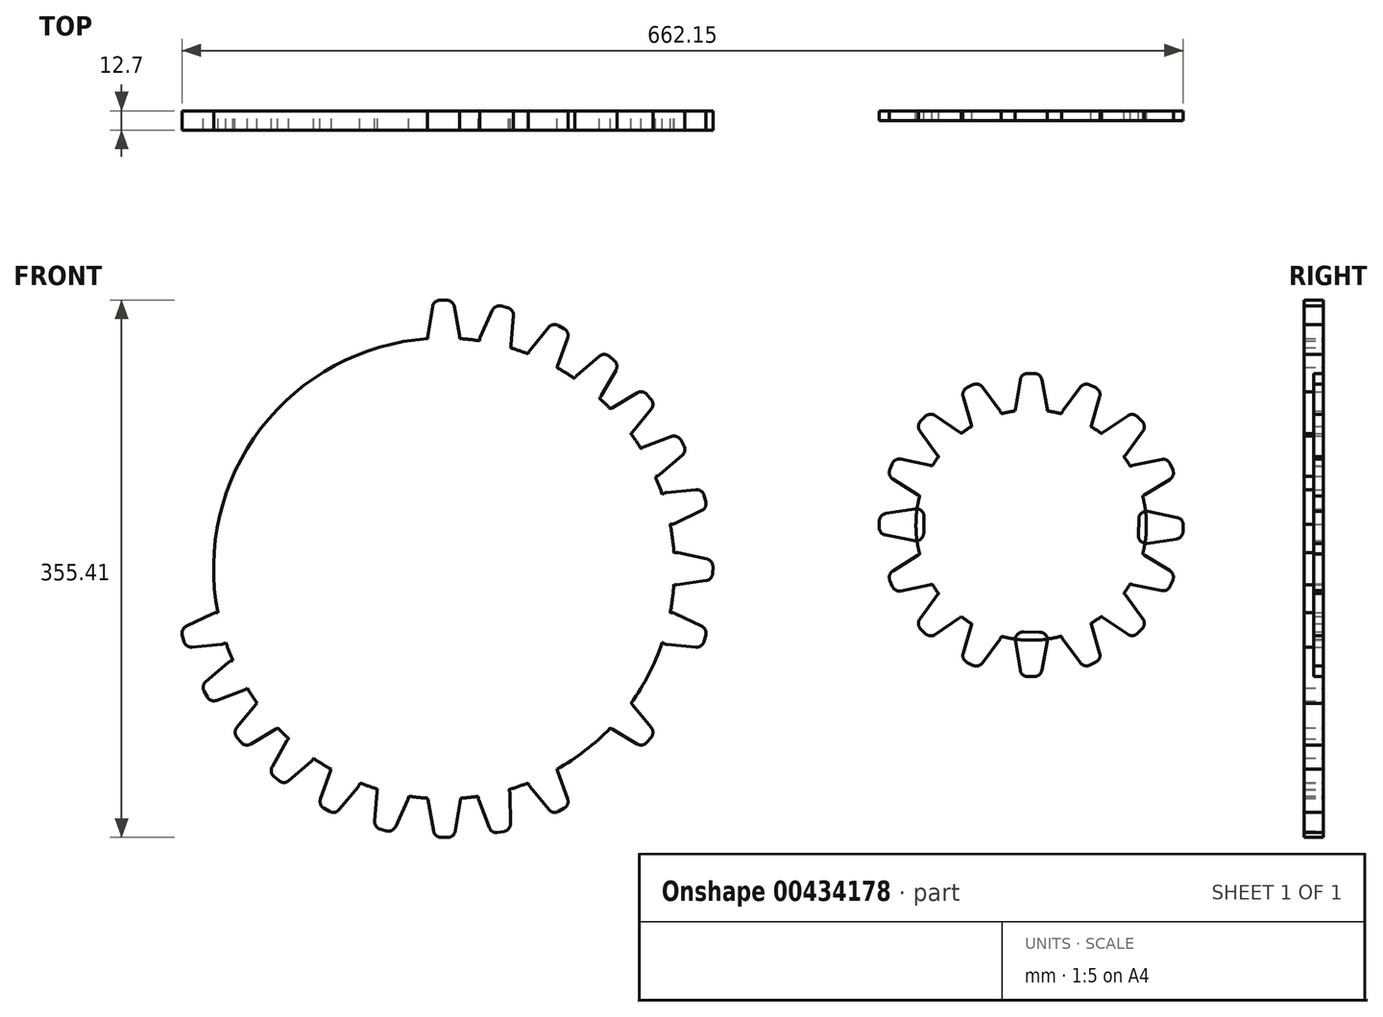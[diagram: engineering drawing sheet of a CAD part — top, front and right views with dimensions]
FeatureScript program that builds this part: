
annotation { "Feature Type Name" : "Feature", "Feature Type Description" : "" }
export const myFeature = defineFeature(function(context is Context, id is Id, definition is map)
    precondition{}
    {
        {
            var Q0;
            Q0=qCreatedBy(makeId("Front.planeOp"),FACE);
            var sketch = newSketch(context, id + "F0", { "sketchPlane" : qUnion([Q0])});
            skCircle(sketch, "E0", {"center": v(0, 0) * mm, "radius": 6.35 * mm});
            skCircle(sketch, "E1", {"center": v(0, 0) * mm, "radius": 152.4 * mm});
            skCircle(sketch, "E2", {"center": v(388.27, 28.72) * mm, "radius": 6.35 * mm});
            skCircle(sketch, "E3", {"center": v(388.27, 28.72) * mm, "radius": 76.2 * mm});
            skLineSegment(sketch, "E4", {"start": v(0, 0) * mm, "end": v(0, -152.4) * mm});
            skLineSegment(sketch, "E5", {"start": v(0, 0) * mm, "end": v(152.4, 0) * mm});
            skLineSegment(sketch, "E6", {"start": v(0, 0) * mm, "end": v(-152.4, 0) * mm});
            skLineSegment(sketch, "E7", {"start": v(37.99, 173.6) * mm, "end": v(42.15, 172.48) * mm});
            skLineSegment(sketch, "E8", {"start": v(45.9, 167.19) * mm, "end": v(44.4, 147.67) * mm});
            skLineSegment(sketch, "E9", {"start": v(32.05, 170.78) * mm, "end": v(23.95, 152.91) * mm});
            skLineSegment(sketch, "E10", {"start": v(27.31, 145.9) * mm, "end": v(38.08, 143.14) * mm});
            skPoint(sketch, "E11.visualSharp", {"position": v(33.82, 174.7) * mm});
            skArc(sketch, "E11.filletArc", {"start": v(37.99, 173.6) * mm, "mid": v(34.5, 173.28) * mm, "end": v(32.05, 170.78) * mm});
            skPoint(sketch, "E12.visualSharp", {"position": v(46.22, 171.39) * mm});
            skArc(sketch, "E12.filletArc", {"start": v(45.9, 167.19) * mm, "mid": v(44.98, 170.5) * mm, "end": v(42.15, 172.48) * mm});
            skPoint(sketch, "E13.visualSharp", {"position": v(43.94, 141.63) * mm});
            skArc(sketch, "E13.filletArc", {"start": v(38.08, 143.14) * mm, "mid": v(42.3, 143.93) * mm, "end": v(44.4, 147.67) * mm});
            skPoint(sketch, "E14.visualSharp", {"position": v(21.45, 147.4) * mm});
            skArc(sketch, "E14.filletArc", {"start": v(23.95, 152.91) * mm, "mid": v(24, 148.62) * mm, "end": v(27.31, 145.9) * mm});
            skPoint(sketch, "E15.endSnap0", {"position": v(32.7, 144.51) * mm});
            skLineSegment(sketch, "E16", {"start": v(75.72, 160.72) * mm, "end": v(79.45, 158.56) * mm});
            skLineSegment(sketch, "E17", {"start": v(81.7, 152.48) * mm, "end": v(75.21, 134.01) * mm});
            skLineSegment(sketch, "E18", {"start": v(69.26, 159.54) * mm, "end": v(56.8, 144.37) * mm});
            skLineSegment(sketch, "E19", {"start": v(58.24, 136.72) * mm, "end": v(67.93, 131.27) * mm});
            skPoint(sketch, "E20.visualSharp", {"position": v(71.99, 162.87) * mm});
            skArc(sketch, "E20.filletArc", {"start": v(75.72, 160.72) * mm, "mid": v(72.27, 161.31) * mm, "end": v(69.26, 159.54) * mm});
            skPoint(sketch, "E21.visualSharp", {"position": v(83.1, 156.46) * mm});
            skArc(sketch, "E21.filletArc", {"start": v(81.7, 152.48) * mm, "mid": v(81.68, 155.93) * mm, "end": v(79.45, 158.56) * mm});
            skPoint(sketch, "E22.visualSharp", {"position": v(73.2, 128.3) * mm});
            skArc(sketch, "E22.filletArc", {"start": v(67.93, 131.27) * mm, "mid": v(72.2, 130.94) * mm, "end": v(75.21, 134.01) * mm});
            skPoint(sketch, "E23.visualSharp", {"position": v(52.97, 139.7) * mm});
            skArc(sketch, "E23.filletArc", {"start": v(56.8, 144.37) * mm, "mid": v(55.74, 140.21) * mm, "end": v(58.24, 136.72) * mm});
            skPoint(sketch, "E24.endSnap0", {"position": v(63.08, 134) * mm});
            skLineSegment(sketch, "E25", {"start": v(109.2, 140.37) * mm, "end": v(112.5, 137.6) * mm});
            skLineSegment(sketch, "E26", {"start": v(113.66, 131.22) * mm, "end": v(104.06, 114.16) * mm});
            skLineSegment(sketch, "E27", {"start": v(102.63, 140.33) * mm, "end": v(87.74, 127.56) * mm});
            skLineSegment(sketch, "E28", {"start": v(87.82, 119.78) * mm, "end": v(96.41, 112.73) * mm});
            skPoint(sketch, "E29.visualSharp", {"position": v(105.9, 143.14) * mm});
            skArc(sketch, "E29.filletArc", {"start": v(109.2, 140.37) * mm, "mid": v(105.91, 141.56) * mm, "end": v(102.63, 140.33) * mm});
            skPoint(sketch, "E30.visualSharp", {"position": v(115.73, 134.9) * mm});
            skArc(sketch, "E30.filletArc", {"start": v(113.66, 131.22) * mm, "mid": v(114.24, 134.62) * mm, "end": v(112.5, 137.6) * mm});
            skPoint(sketch, "E31.visualSharp", {"position": v(101.1, 108.89) * mm});
            skArc(sketch, "E31.filletArc", {"start": v(96.41, 112.73) * mm, "mid": v(100.57, 111.66) * mm, "end": v(104.06, 114.16) * mm});
            skPoint(sketch, "E32.visualSharp", {"position": v(83.14, 123.62) * mm});
            skArc(sketch, "E32.filletArc", {"start": v(87.74, 127.56) * mm, "mid": v(85.97, 123.65) * mm, "end": v(87.82, 119.78) * mm});
            skPoint(sketch, "E33.endSnap0", {"position": v(92.12, 116.25) * mm});
            skLineSegment(sketch, "E34", {"start": v(134.2, 115.06) * mm, "end": v(136.96, 111.76) * mm});
            skLineSegment(sketch, "E35", {"start": v(137, 105.27) * mm, "end": v(124.58, 90.14) * mm});
            skLineSegment(sketch, "E36", {"start": v(127.72, 116.16) * mm, "end": v(110.83, 106.17) * mm});
            skLineSegment(sketch, "E37", {"start": v(109.56, 98.49) * mm, "end": v(116.8, 90.06) * mm});
            skPoint(sketch, "E38.visualSharp", {"position": v(131.42, 118.36) * mm});
            skArc(sketch, "E38.filletArc", {"start": v(134.2, 115.06) * mm, "mid": v(131.16, 116.8) * mm, "end": v(127.72, 116.16) * mm});
            skPoint(sketch, "E39.visualSharp", {"position": v(139.67, 108.53) * mm});
            skArc(sketch, "E39.filletArc", {"start": v(137, 105.27) * mm, "mid": v(138.15, 108.52) * mm, "end": v(136.96, 111.76) * mm});
            skPoint(sketch, "E40.visualSharp", {"position": v(120.74, 85.46) * mm});
            skArc(sketch, "E40.filletArc", {"start": v(116.8, 90.06) * mm, "mid": v(120.7, 88.28) * mm, "end": v(124.58, 90.14) * mm});
            skPoint(sketch, "E41.visualSharp", {"position": v(105.62, 103.08) * mm});
            skArc(sketch, "E41.filletArc", {"start": v(110.83, 106.17) * mm, "mid": v(108.4, 102.62) * mm, "end": v(109.56, 98.49) * mm});
            skPoint(sketch, "E42.endSnap0", {"position": v(113.18, 94.27) * mm});
            skLineSegment(sketch, "E43", {"start": v(156.51, 85.04) * mm, "end": v(158.66, 81.31) * mm});
            skLineSegment(sketch, "E44", {"start": v(157.57, 74.92) * mm, "end": v(142.72, 62.17) * mm});
            skLineSegment(sketch, "E45", {"start": v(150.32, 87.26) * mm, "end": v(131.96, 80.34) * mm});
            skLineSegment(sketch, "E46", {"start": v(129.38, 73) * mm, "end": v(135.04, 63.44) * mm});
            skPoint(sketch, "E47.visualSharp", {"position": v(154.36, 88.77) * mm});
            skArc(sketch, "E47.filletArc", {"start": v(156.51, 85.04) * mm, "mid": v(153.82, 87.28) * mm, "end": v(150.32, 87.26) * mm});
            skPoint(sketch, "E48.visualSharp", {"position": v(160.77, 77.66) * mm});
            skArc(sketch, "E48.filletArc", {"start": v(157.57, 74.92) * mm, "mid": v(159.27, 77.92) * mm, "end": v(158.66, 81.31) * mm});
            skPoint(sketch, "E49.visualSharp", {"position": v(138.12, 58.23) * mm});
            skArc(sketch, "E49.filletArc", {"start": v(135.04, 63.44) * mm, "mid": v(138.58, 61.02) * mm, "end": v(142.72, 62.17) * mm});
            skPoint(sketch, "E50.visualSharp", {"position": v(126.3, 78.21) * mm});
            skArc(sketch, "E50.filletArc", {"start": v(131.96, 80.34) * mm, "mid": v(128.96, 77.27) * mm, "end": v(129.38, 73) * mm});
            skPoint(sketch, "E51.endSnap0", {"position": v(132.2, 68.22) * mm});
            skLineSegment(sketch, "E52", {"start": v(172.02, 48.32) * mm, "end": v(173.13, 44.16) * mm});
            skLineSegment(sketch, "E53", {"start": v(170.42, 38.26) * mm, "end": v(152.77, 29.8) * mm});
            skLineSegment(sketch, "E54", {"start": v(166.61, 52.06) * mm, "end": v(147.09, 50.13) * mm});
            skLineSegment(sketch, "E55", {"start": v(142.7, 43.7) * mm, "end": v(145.68, 33) * mm});
            skPoint(sketch, "E56.visualSharp", {"position": v(170.9, 52.48) * mm});
            skArc(sketch, "E56.filletArc", {"start": v(172.02, 48.32) * mm, "mid": v(170, 51.18) * mm, "end": v(166.61, 52.06) * mm});
            skPoint(sketch, "E57.visualSharp", {"position": v(174.22, 40.08) * mm});
            skArc(sketch, "E57.filletArc", {"start": v(170.42, 38.26) * mm, "mid": v(172.84, 40.72) * mm, "end": v(173.13, 44.16) * mm});
            skPoint(sketch, "E58.visualSharp", {"position": v(147.31, 27.18) * mm});
            skArc(sketch, "E58.filletArc", {"start": v(145.68, 33) * mm, "mid": v(148.48, 29.75) * mm, "end": v(152.77, 29.8) * mm});
            skPoint(sketch, "E59.visualSharp", {"position": v(141.06, 49.54) * mm});
            skArc(sketch, "E59.filletArc", {"start": v(147.09, 50.13) * mm, "mid": v(143.4, 47.95) * mm, "end": v(142.7, 43.7) * mm});
            skPoint(sketch, "E60.endSnap0", {"position": v(144.19, 38.36) * mm});
            skArc(sketch, "E61.MirrorCS", {"start": v(-45.9, 167.19) * mm, "mid": v(-44.98, 170.5) * mm, "end": v(-42.15, 172.48) * mm});
            skArc(sketch, "E62.MirrorCS", {"start": v(-113.66, 131.22) * mm, "mid": v(-114.24, 134.62) * mm, "end": v(-112.5, 137.6) * mm});
            skArc(sketch, "E63.MirrorCS", {"start": v(-157.57, 74.92) * mm, "mid": v(-159.27, 77.92) * mm, "end": v(-158.66, 81.31) * mm});
            skArc(sketch, "E64.MirrorCS", {"start": v(-75.72, 160.72) * mm, "mid": v(-72.27, 161.31) * mm, "end": v(-69.26, 159.54) * mm});
            skArc(sketch, "E65.MirrorCS", {"start": v(-134.2, 115.06) * mm, "mid": v(-131.16, 116.8) * mm, "end": v(-127.72, 116.16) * mm});
            skArc(sketch, "E66.MirrorCS", {"start": v(-170.42, 38.26) * mm, "mid": v(-172.84, 40.72) * mm, "end": v(-173.13, 44.16) * mm});
            skLineSegment(sketch, "E67.MirrorCS", {"start": v(-156.51, 85.04) * mm, "end": v(-158.66, 81.31) * mm});
            skLineSegment(sketch, "E68.MirrorCS", {"start": v(-134.2, 115.06) * mm, "end": v(-136.96, 111.76) * mm});
            skLineSegment(sketch, "E69.MirrorCS", {"start": v(-37.99, 173.6) * mm, "end": v(-42.15, 172.48) * mm});
            skLineSegment(sketch, "E70.MirrorCS", {"start": v(-109.2, 140.37) * mm, "end": v(-112.5, 137.6) * mm});
            skLineSegment(sketch, "E71.MirrorCS", {"start": v(-75.72, 160.72) * mm, "end": v(-79.45, 158.56) * mm});
            skLineSegment(sketch, "E72.MirrorCS", {"start": v(-172.02, 48.32) * mm, "end": v(-173.13, 44.16) * mm});
            skArc(sketch, "E73.MirrorCS", {"start": v(-109.2, 140.37) * mm, "mid": v(-105.91, 141.56) * mm, "end": v(-102.63, 140.33) * mm});
            skArc(sketch, "E74.MirrorCS", {"start": v(-137, 105.27) * mm, "mid": v(-138.15, 108.52) * mm, "end": v(-136.96, 111.76) * mm});
            skArc(sketch, "E75.MirrorCS", {"start": v(-37.99, 173.6) * mm, "mid": v(-34.5, 173.28) * mm, "end": v(-32.05, 170.78) * mm});
            skArc(sketch, "E76.MirrorCS", {"start": v(-156.51, 85.04) * mm, "mid": v(-153.82, 87.28) * mm, "end": v(-150.32, 87.26) * mm});
            skArc(sketch, "E77.MirrorCS", {"start": v(-81.7, 152.48) * mm, "mid": v(-81.68, 155.93) * mm, "end": v(-79.45, 158.56) * mm});
            skArc(sketch, "E78.MirrorCS", {"start": v(-67.93, 131.27) * mm, "mid": v(-72.2, 130.94) * mm, "end": v(-75.21, 134.01) * mm});
            skArc(sketch, "E79.MirrorCS", {"start": v(-116.8, 90.06) * mm, "mid": v(-120.7, 88.28) * mm, "end": v(-124.58, 90.14) * mm});
            skArc(sketch, "E80.MirrorCS", {"start": v(-145.68, 33) * mm, "mid": v(-148.48, 29.75) * mm, "end": v(-152.77, 29.8) * mm});
            skArc(sketch, "E81.MirrorCS", {"start": v(-135.04, 63.44) * mm, "mid": v(-138.58, 61.02) * mm, "end": v(-142.72, 62.17) * mm});
            skArc(sketch, "E82.MirrorCS", {"start": v(-96.41, 112.73) * mm, "mid": v(-100.57, 111.66) * mm, "end": v(-104.06, 114.16) * mm});
            skArc(sketch, "E83.MirrorCS", {"start": v(-38.08, 143.14) * mm, "mid": v(-42.3, 143.93) * mm, "end": v(-44.4, 147.67) * mm});
            skArc(sketch, "E84.MirrorCS", {"start": v(-147.09, 50.13) * mm, "mid": v(-143.4, 47.95) * mm, "end": v(-142.7, 43.7) * mm});
            skArc(sketch, "E85.MirrorCS", {"start": v(-110.83, 106.17) * mm, "mid": v(-108.4, 102.62) * mm, "end": v(-109.56, 98.49) * mm});
            skArc(sketch, "E86.MirrorCS", {"start": v(-56.8, 144.37) * mm, "mid": v(-55.74, 140.21) * mm, "end": v(-58.24, 136.72) * mm});
            skArc(sketch, "E87.MirrorCS", {"start": v(-172.02, 48.32) * mm, "mid": v(-170, 51.18) * mm, "end": v(-166.61, 52.06) * mm});
            skLineSegment(sketch, "E88.MirrorCS", {"start": v(-142.7, 43.7) * mm, "end": v(-145.68, 33) * mm});
            skLineSegment(sketch, "E89.MirrorCS", {"start": v(-109.56, 98.49) * mm, "end": v(-116.8, 90.06) * mm});
            skLineSegment(sketch, "E90.MirrorCS", {"start": v(-58.24, 136.72) * mm, "end": v(-67.93, 131.27) * mm});
            skLineSegment(sketch, "E91.MirrorCS", {"start": v(-27.31, 145.9) * mm, "end": v(-38.08, 143.14) * mm});
            skArc(sketch, "E92.MirrorCS", {"start": v(-87.74, 127.56) * mm, "mid": v(-85.97, 123.65) * mm, "end": v(-87.82, 119.78) * mm});
            skArc(sketch, "E93.MirrorCS", {"start": v(-23.95, 152.91) * mm, "mid": v(-24, 148.62) * mm, "end": v(-27.31, 145.9) * mm});
            skArc(sketch, "E94.MirrorCS", {"start": v(-131.96, 80.34) * mm, "mid": v(-128.96, 77.27) * mm, "end": v(-129.38, 73) * mm});
            skLineSegment(sketch, "E95.MirrorCS", {"start": v(-87.82, 119.78) * mm, "end": v(-96.41, 112.73) * mm});
            skLineSegment(sketch, "E96.MirrorCS", {"start": v(-129.38, 73) * mm, "end": v(-135.04, 63.44) * mm});
            skPoint(sketch, "E97.MirrorP", {"position": v(-132.2, 68.22) * mm});
            skPoint(sketch, "E98.MirrorP", {"position": v(-144.19, 38.36) * mm});
            skPoint(sketch, "E99.MirrorP", {"position": v(-160.77, 77.66) * mm});
            skPoint(sketch, "E100.MirrorP", {"position": v(-101.1, 108.89) * mm});
            skPoint(sketch, "E101.MirrorP", {"position": v(-21.45, 147.4) * mm});
            skPoint(sketch, "E102.MirrorP", {"position": v(-73.2, 128.3) * mm});
            skPoint(sketch, "E103.MirrorP", {"position": v(-141.06, 49.54) * mm});
            skPoint(sketch, "E104.MirrorP", {"position": v(-113.18, 94.27) * mm});
            skPoint(sketch, "E105.MirrorP", {"position": v(-71.99, 162.87) * mm});
            skPoint(sketch, "E106.MirrorP", {"position": v(-46.22, 171.39) * mm});
            skLineSegment(sketch, "E107.MirrorCS", {"start": v(-170.42, 38.26) * mm, "end": v(-152.77, 29.8) * mm});
            skPoint(sketch, "E108.MirrorP", {"position": v(-154.36, 88.77) * mm});
            skPoint(sketch, "E109.MirrorP", {"position": v(-52.97, 139.7) * mm});
            skLineSegment(sketch, "E110.MirrorCS", {"start": v(-32.05, 170.78) * mm, "end": v(-23.95, 152.91) * mm});
            skPoint(sketch, "E111.MirrorP", {"position": v(-115.73, 134.9) * mm});
            skLineSegment(sketch, "E112.MirrorCS", {"start": v(-137, 105.27) * mm, "end": v(-124.58, 90.14) * mm});
            skPoint(sketch, "E113.MirrorP", {"position": v(-83.1, 156.46) * mm});
            skLineSegment(sketch, "E114.MirrorCS", {"start": v(-102.63, 140.33) * mm, "end": v(-87.74, 127.56) * mm});
            skLineSegment(sketch, "E115.MirrorCS", {"start": v(-150.32, 87.26) * mm, "end": v(-131.96, 80.34) * mm});
            skPoint(sketch, "E116.MirrorP", {"position": v(-63.08, 134) * mm});
            skPoint(sketch, "E117.MirrorP", {"position": v(-138.12, 58.23) * mm});
            skLineSegment(sketch, "E118.MirrorCS", {"start": v(-113.66, 131.22) * mm, "end": v(-104.06, 114.16) * mm});
            skLineSegment(sketch, "E119.MirrorCS", {"start": v(-127.72, 116.16) * mm, "end": v(-110.83, 106.17) * mm});
            skPoint(sketch, "E120.MirrorP", {"position": v(-43.94, 141.63) * mm});
            skLineSegment(sketch, "E121.MirrorCS", {"start": v(-157.57, 74.92) * mm, "end": v(-142.72, 62.17) * mm});
            skPoint(sketch, "E122.MirrorP", {"position": v(-170.9, 52.48) * mm});
            skPoint(sketch, "E123.MirrorP", {"position": v(-105.9, 143.14) * mm});
            skLineSegment(sketch, "E124.MirrorCS", {"start": v(-81.7, 152.48) * mm, "end": v(-75.21, 134.01) * mm});
            skPoint(sketch, "E125.MirrorP", {"position": v(-120.74, 85.46) * mm});
            skPoint(sketch, "E126.MirrorP", {"position": v(-32.7, 144.51) * mm});
            skPoint(sketch, "E127.MirrorP", {"position": v(-83.14, 123.62) * mm});
            skPoint(sketch, "E128.MirrorP", {"position": v(-174.22, 40.08) * mm});
            skPoint(sketch, "E129.MirrorP", {"position": v(-131.42, 118.36) * mm});
            skPoint(sketch, "E130.MirrorP", {"position": v(-33.82, 174.7) * mm});
            skPoint(sketch, "E131.MirrorP", {"position": v(-139.67, 108.53) * mm});
            skLineSegment(sketch, "E132.MirrorCS", {"start": v(-69.26, 159.54) * mm, "end": v(-56.8, 144.37) * mm});
            skLineSegment(sketch, "E133.MirrorCS", {"start": v(-45.9, 167.19) * mm, "end": v(-44.4, 147.67) * mm});
            skPoint(sketch, "E134.MirrorP", {"position": v(-147.31, 27.18) * mm});
            skLineSegment(sketch, "E135.MirrorCS", {"start": v(-166.61, 52.06) * mm, "end": v(-147.09, 50.13) * mm});
            skPoint(sketch, "E136.MirrorP", {"position": v(-105.62, 103.08) * mm});
            skPoint(sketch, "E137.MirrorP", {"position": v(-126.3, 78.21) * mm});
            skPoint(sketch, "E138.MirrorP", {"position": v(-92.12, 116.25) * mm});
            skArc(sketch, "E139.MirrorCS", {"start": v(-56.8, -144.37) * mm, "mid": v(-55.74, -140.21) * mm, "end": v(-58.24, -136.72) * mm});
            skLineSegment(sketch, "E140.MirrorCS", {"start": v(134.2, -115.06) * mm, "end": v(136.96, -111.76) * mm});
            skLineSegment(sketch, "E141.MirrorCS", {"start": v(75.72, -160.72) * mm, "end": v(79.45, -158.56) * mm});
            skArc(sketch, "E142.MirrorCS", {"start": v(81.7, -152.48) * mm, "mid": v(81.68, -155.93) * mm, "end": v(79.45, -158.56) * mm});
            skArc(sketch, "E143.MirrorCS", {"start": v(75.72, -160.72) * mm, "mid": v(72.27, -161.31) * mm, "end": v(69.26, -159.54) * mm});
            skLineSegment(sketch, "E144.MirrorCS", {"start": v(129.38, -73) * mm, "end": v(135.04, -63.44) * mm});
            skLineSegment(sketch, "E145.MirrorCS", {"start": v(87.82, -119.78) * mm, "end": v(96.41, -112.73) * mm});
            skLineSegment(sketch, "E146.MirrorCS", {"start": v(-109.2, -140.37) * mm, "end": v(-112.5, -137.6) * mm});
            skArc(sketch, "E147.MirrorCS", {"start": v(157.57, -74.92) * mm, "mid": v(159.27, -77.92) * mm, "end": v(158.66, -81.31) * mm});
            skArc(sketch, "E148.MirrorCS", {"start": v(135.04, -63.44) * mm, "mid": v(138.58, -61.02) * mm, "end": v(142.72, -62.17) * mm});
            skArc(sketch, "E149.MirrorCS", {"start": v(96.41, -112.73) * mm, "mid": v(100.57, -111.66) * mm, "end": v(104.06, -114.16) * mm});
            skArc(sketch, "E150.MirrorCS", {"start": v(131.96, -80.34) * mm, "mid": v(128.96, -77.27) * mm, "end": v(129.38, -73) * mm});
            skArc(sketch, "E151.MirrorCS", {"start": v(87.74, -127.56) * mm, "mid": v(85.97, -123.65) * mm, "end": v(87.82, -119.78) * mm});
            skArc(sketch, "E152.MirrorCS", {"start": v(-137, -105.27) * mm, "mid": v(-138.15, -108.52) * mm, "end": v(-136.96, -111.76) * mm});
            skLineSegment(sketch, "E153.MirrorCS", {"start": v(127.72, -116.16) * mm, "end": v(110.83, -106.17) * mm});
            skLineSegment(sketch, "E154.MirrorCS", {"start": v(69.26, -159.54) * mm, "end": v(56.8, -144.37) * mm});
            skArc(sketch, "E155.MirrorCS", {"start": v(145.68, -33) * mm, "mid": v(148.48, -29.75) * mm, "end": v(152.77, -29.8) * mm});
            skLineSegment(sketch, "E156.MirrorCS", {"start": v(-134.2, -115.06) * mm, "end": v(-136.96, -111.76) * mm});
            skArc(sketch, "E157.MirrorCS", {"start": v(110.83, -106.17) * mm, "mid": v(108.4, -102.62) * mm, "end": v(109.56, -98.49) * mm});
            skArc(sketch, "E158.MirrorCS", {"start": v(147.09, -50.13) * mm, "mid": v(143.4, -47.95) * mm, "end": v(142.7, -43.7) * mm});
            skArc(sketch, "E159.MirrorCS", {"start": v(56.8, -144.37) * mm, "mid": v(55.74, -140.21) * mm, "end": v(58.24, -136.72) * mm});
            skArc(sketch, "E160.MirrorCS", {"start": v(-145.68, -33) * mm, "mid": v(-148.48, -29.75) * mm, "end": v(-152.77, -29.8) * mm});
            skArc(sketch, "E161.MirrorCS", {"start": v(-134.2, -115.06) * mm, "mid": v(-131.16, -116.8) * mm, "end": v(-127.72, -116.16) * mm});
            skArc(sketch, "E162.MirrorCS", {"start": v(137, -105.27) * mm, "mid": v(138.15, -108.52) * mm, "end": v(136.96, -111.76) * mm});
            skLineSegment(sketch, "E163.MirrorCS", {"start": v(142.7, -43.7) * mm, "end": v(145.68, -33) * mm});
            skArc(sketch, "E164.MirrorCS", {"start": v(134.2, -115.06) * mm, "mid": v(131.16, -116.8) * mm, "end": v(127.72, -116.16) * mm});
            skLineSegment(sketch, "E165.MirrorCS", {"start": v(-81.7, -152.48) * mm, "end": v(-75.21, -134.01) * mm});
            skArc(sketch, "E166.MirrorCS", {"start": v(156.51, -85.04) * mm, "mid": v(153.82, -87.28) * mm, "end": v(150.32, -87.26) * mm});
            skArc(sketch, "E167.MirrorCS", {"start": v(109.2, -140.37) * mm, "mid": v(105.91, -141.56) * mm, "end": v(102.63, -140.33) * mm});
            skArc(sketch, "E168.MirrorCS", {"start": v(-131.96, -80.34) * mm, "mid": v(-128.96, -77.27) * mm, "end": v(-129.38, -73) * mm});
            skLineSegment(sketch, "E169.MirrorCS", {"start": v(-75.72, -160.72) * mm, "end": v(-79.45, -158.56) * mm});
            skArc(sketch, "E170.MirrorCS", {"start": v(113.66, -131.22) * mm, "mid": v(114.24, -134.62) * mm, "end": v(112.5, -137.6) * mm});
            skLineSegment(sketch, "E171.MirrorCS", {"start": v(-69.26, -159.54) * mm, "end": v(-56.8, -144.37) * mm});
            skArc(sketch, "E172.MirrorCS", {"start": v(-110.83, -106.17) * mm, "mid": v(-108.4, -102.62) * mm, "end": v(-109.56, -98.49) * mm});
            skLineSegment(sketch, "E173.MirrorCS", {"start": v(-172.02, -48.32) * mm, "end": v(-173.13, -44.16) * mm});
            skLineSegment(sketch, "E174.MirrorCS", {"start": v(-129.38, -73) * mm, "end": v(-135.04, -63.44) * mm});
            skArc(sketch, "E175.MirrorCS", {"start": v(-172.02, -48.32) * mm, "mid": v(-170, -51.18) * mm, "end": v(-166.61, -52.06) * mm});
            skArc(sketch, "E176.MirrorCS", {"start": v(-109.2, -140.37) * mm, "mid": v(-105.91, -141.56) * mm, "end": v(-102.63, -140.33) * mm});
            skLineSegment(sketch, "E177.MirrorCS", {"start": v(172.02, -48.32) * mm, "end": v(173.13, -44.16) * mm});
            skLineSegment(sketch, "E178.MirrorCS", {"start": v(170.42, -38.26) * mm, "end": v(152.77, -29.8) * mm});
            skLineSegment(sketch, "E179.MirrorCS", {"start": v(137, -105.27) * mm, "end": v(124.58, -90.14) * mm});
            skLineSegment(sketch, "E180.MirrorCS", {"start": v(81.7, -152.48) * mm, "end": v(75.21, -134.01) * mm});
            skLineSegment(sketch, "E181.MirrorCS", {"start": v(166.61, -52.06) * mm, "end": v(147.09, -50.13) * mm});
            skArc(sketch, "E182.MirrorCS", {"start": v(-113.66, -131.22) * mm, "mid": v(-114.24, -134.62) * mm, "end": v(-112.5, -137.6) * mm});
            skArc(sketch, "E183.MirrorCS", {"start": v(67.93, -131.27) * mm, "mid": v(72.2, -130.94) * mm, "end": v(75.21, -134.01) * mm});
            skArc(sketch, "E184.MirrorCS", {"start": v(116.8, -90.06) * mm, "mid": v(120.7, -88.28) * mm, "end": v(124.58, -90.14) * mm});
            skArc(sketch, "E185.MirrorCS", {"start": v(-170.42, -38.26) * mm, "mid": v(-172.84, -40.72) * mm, "end": v(-173.13, -44.16) * mm});
            skLineSegment(sketch, "E186.MirrorCS", {"start": v(113.66, -131.22) * mm, "end": v(104.06, -114.16) * mm});
            skLineSegment(sketch, "E187.MirrorCS", {"start": v(-157.57, -74.92) * mm, "end": v(-142.72, -62.17) * mm});
            skLineSegment(sketch, "E188.MirrorCS", {"start": v(102.63, -140.33) * mm, "end": v(87.74, -127.56) * mm});
            skLineSegment(sketch, "E189.MirrorCS", {"start": v(58.24, -136.72) * mm, "end": v(67.93, -131.27) * mm});
            skLineSegment(sketch, "E190.MirrorCS", {"start": v(-150.32, -87.26) * mm, "end": v(-131.96, -80.34) * mm});
            skLineSegment(sketch, "E191.MirrorCS", {"start": v(-156.51, -85.04) * mm, "end": v(-158.66, -81.31) * mm});
            skArc(sketch, "E192.MirrorCS", {"start": v(-67.93, -131.27) * mm, "mid": v(-72.2, -130.94) * mm, "end": v(-75.21, -134.01) * mm});
            skArc(sketch, "E193.MirrorCS", {"start": v(-75.72, -160.72) * mm, "mid": v(-72.27, -161.31) * mm, "end": v(-69.26, -159.54) * mm});
            skArc(sketch, "E194.MirrorCS", {"start": v(-81.7, -152.48) * mm, "mid": v(-81.68, -155.93) * mm, "end": v(-79.45, -158.56) * mm});
            skArc(sketch, "E195.MirrorCS", {"start": v(-157.57, -74.92) * mm, "mid": v(-159.27, -77.92) * mm, "end": v(-158.66, -81.31) * mm});
            skLineSegment(sketch, "E196.MirrorCS", {"start": v(109.2, -140.37) * mm, "end": v(112.5, -137.6) * mm});
            skLineSegment(sketch, "E197.MirrorCS", {"start": v(156.51, -85.04) * mm, "end": v(158.66, -81.31) * mm});
            skLineSegment(sketch, "E198.MirrorCS", {"start": v(-127.72, -116.16) * mm, "end": v(-110.83, -106.17) * mm});
            skArc(sketch, "E199.MirrorCS", {"start": v(-96.41, -112.73) * mm, "mid": v(-100.57, -111.66) * mm, "end": v(-104.06, -114.16) * mm});
            skLineSegment(sketch, "E200.MirrorCS", {"start": v(109.56, -98.49) * mm, "end": v(116.8, -90.06) * mm});
            skArc(sketch, "E201.MirrorCS", {"start": v(-156.51, -85.04) * mm, "mid": v(-153.82, -87.28) * mm, "end": v(-150.32, -87.26) * mm});
            skLineSegment(sketch, "E202.MirrorCS", {"start": v(-113.66, -131.22) * mm, "end": v(-104.06, -114.16) * mm});
            skLineSegment(sketch, "E203.MirrorCS", {"start": v(-58.24, -136.72) * mm, "end": v(-67.93, -131.27) * mm});
            skLineSegment(sketch, "E204.MirrorCS", {"start": v(157.57, -74.92) * mm, "end": v(142.72, -62.17) * mm});
            skArc(sketch, "E205.MirrorCS", {"start": v(-135.04, -63.44) * mm, "mid": v(-138.58, -61.02) * mm, "end": v(-142.72, -62.17) * mm});
            skLineSegment(sketch, "E206.MirrorCS", {"start": v(150.32, -87.26) * mm, "end": v(131.96, -80.34) * mm});
            skArc(sketch, "E207.MirrorCS", {"start": v(172.02, -48.32) * mm, "mid": v(170, -51.18) * mm, "end": v(166.61, -52.06) * mm});
            skArc(sketch, "E208.MirrorCS", {"start": v(170.42, -38.26) * mm, "mid": v(172.84, -40.72) * mm, "end": v(173.13, -44.16) * mm});
            skPoint(sketch, "E209.MirrorP", {"position": v(71.99, -162.87) * mm});
            skArc(sketch, "E210.MirrorCS", {"start": v(-147.09, -50.13) * mm, "mid": v(-143.4, -47.95) * mm, "end": v(-142.7, -43.7) * mm});
            skPoint(sketch, "E211.MirrorP", {"position": v(-71.99, -162.87) * mm});
            skLineSegment(sketch, "E212.MirrorCS", {"start": v(-87.82, -119.78) * mm, "end": v(-96.41, -112.73) * mm});
            skLineSegment(sketch, "E213.MirrorCS", {"start": v(-170.42, -38.26) * mm, "end": v(-152.77, -29.8) * mm});
            skLineSegment(sketch, "E214.MirrorCS", {"start": v(-166.61, -52.06) * mm, "end": v(-147.09, -50.13) * mm});
            skArc(sketch, "E215.MirrorCS", {"start": v(-116.8, -90.06) * mm, "mid": v(-120.7, -88.28) * mm, "end": v(-124.58, -90.14) * mm});
            skLineSegment(sketch, "E216.MirrorCS", {"start": v(-109.56, -98.49) * mm, "end": v(-116.8, -90.06) * mm});
            skLineSegment(sketch, "E217.MirrorCS", {"start": v(-137, -105.27) * mm, "end": v(-124.58, -90.14) * mm});
            skArc(sketch, "E218.MirrorCS", {"start": v(-87.74, -127.56) * mm, "mid": v(-85.97, -123.65) * mm, "end": v(-87.82, -119.78) * mm});
            skLineSegment(sketch, "E219.MirrorCS", {"start": v(-102.63, -140.33) * mm, "end": v(-87.74, -127.56) * mm});
            skLineSegment(sketch, "E220.MirrorCS", {"start": v(-142.7, -43.7) * mm, "end": v(-145.68, -33) * mm});
            skPoint(sketch, "E221.MirrorP", {"position": v(-174.22, -40.08) * mm});
            skPoint(sketch, "E222.MirrorP", {"position": v(139.67, -108.53) * mm});
            skPoint(sketch, "E223.MirrorP", {"position": v(-52.97, -139.7) * mm});
            skPoint(sketch, "E224.MirrorP", {"position": v(174.22, -40.08) * mm});
            skPoint(sketch, "E225.MirrorP", {"position": v(52.97, -139.7) * mm});
            skPoint(sketch, "E226.MirrorP", {"position": v(113.18, -94.27) * mm});
            skPoint(sketch, "E227.MirrorP", {"position": v(160.77, -77.66) * mm});
            skPoint(sketch, "E228.MirrorP", {"position": v(141.06, -49.54) * mm});
            skPoint(sketch, "E229.MirrorP", {"position": v(-105.9, -143.14) * mm});
            skPoint(sketch, "E230.MirrorP", {"position": v(138.12, -58.23) * mm});
            skPoint(sketch, "E231.MirrorP", {"position": v(83.14, -123.62) * mm});
            skPoint(sketch, "E232.MirrorP", {"position": v(-141.06, -49.54) * mm});
            skPoint(sketch, "E233.MirrorP", {"position": v(-113.18, -94.27) * mm});
            skPoint(sketch, "E234.MirrorP", {"position": v(-120.74, -85.46) * mm});
            skPoint(sketch, "E235.MirrorP", {"position": v(126.3, -78.21) * mm});
            skPoint(sketch, "E236.MirrorP", {"position": v(92.12, -116.25) * mm});
            skPoint(sketch, "E237.MirrorP", {"position": v(131.42, -118.36) * mm});
            skPoint(sketch, "E238.MirrorP", {"position": v(83.1, -156.46) * mm});
            skPoint(sketch, "E239.MirrorP", {"position": v(-83.14, -123.62) * mm});
            skPoint(sketch, "E240.MirrorP", {"position": v(132.2, -68.22) * mm});
            skPoint(sketch, "E241.MirrorP", {"position": v(-154.36, -88.77) * mm});
            skPoint(sketch, "E242.MirrorP", {"position": v(73.2, -128.3) * mm});
            skPoint(sketch, "E243.MirrorP", {"position": v(170.9, -52.48) * mm});
            skPoint(sketch, "E244.MirrorP", {"position": v(-131.42, -118.36) * mm});
            skPoint(sketch, "E245.MirrorP", {"position": v(-115.73, -134.9) * mm});
            skPoint(sketch, "E246.MirrorP", {"position": v(120.74, -85.46) * mm});
            skPoint(sketch, "E247.MirrorP", {"position": v(-139.67, -108.53) * mm});
            skPoint(sketch, "E248.MirrorP", {"position": v(-132.2, -68.22) * mm});
            skPoint(sketch, "E249.MirrorP", {"position": v(63.08, -134) * mm});
            skPoint(sketch, "E250.MirrorP", {"position": v(105.62, -103.08) * mm});
            skPoint(sketch, "E251.MirrorP", {"position": v(-63.08, -134) * mm});
            skPoint(sketch, "E252.MirrorP", {"position": v(-144.19, -38.36) * mm});
            skPoint(sketch, "E253.MirrorP", {"position": v(-92.12, -116.25) * mm});
            skPoint(sketch, "E254.MirrorP", {"position": v(-170.9, -52.48) * mm});
            skPoint(sketch, "E255.MirrorP", {"position": v(-73.2, -128.3) * mm});
            skPoint(sketch, "E256.MirrorP", {"position": v(101.1, -108.89) * mm});
            skPoint(sketch, "E257.MirrorP", {"position": v(-105.62, -103.08) * mm});
            skPoint(sketch, "E258.MirrorP", {"position": v(-160.77, -77.66) * mm});
            skPoint(sketch, "E259.MirrorP", {"position": v(-126.3, -78.21) * mm});
            skPoint(sketch, "E260.MirrorP", {"position": v(105.9, -143.14) * mm});
            skPoint(sketch, "E261.MirrorP", {"position": v(154.36, -88.77) * mm});
            skPoint(sketch, "E262.MirrorP", {"position": v(-83.1, -156.46) * mm});
            skPoint(sketch, "E263.MirrorP", {"position": v(115.73, -134.9) * mm});
            skPoint(sketch, "E264.MirrorP", {"position": v(-101.1, -108.89) * mm});
            skPoint(sketch, "E265.MirrorP", {"position": v(-147.31, -27.18) * mm});
            skPoint(sketch, "E266.MirrorP", {"position": v(144.19, -38.36) * mm});
            skPoint(sketch, "E267.MirrorP", {"position": v(-138.12, -58.23) * mm});
            skLineSegment(sketch, "E268", {"start": v(2.47, -177.95) * mm, "end": v(-1.84, -177.95) * mm});
            skLineSegment(sketch, "E269", {"start": v(-6.83, -173.8) * mm, "end": v(-10.78, -152.73) * mm});
            skLineSegment(sketch, "E270", {"start": v(7.48, -173.7) * mm, "end": v(10.98, -152.5) * mm});
            skLineSegment(sketch, "E271", {"start": v(5.91, -146.59) * mm, "end": v(-5.85, -146.72) * mm});
            skPoint(sketch, "E272.visualSharp", {"position": v(6.78, -177.95) * mm});
            skArc(sketch, "E272.filletArc", {"start": v(2.47, -177.95) * mm, "mid": v(5.76, -176.74) * mm, "end": v(7.48, -173.7) * mm});
            skPoint(sketch, "E273.visualSharp", {"position": v(-6.05, -177.95) * mm});
            skArc(sketch, "E273.filletArc", {"start": v(-6.83, -173.8) * mm, "mid": v(-5.08, -176.78) * mm, "end": v(-1.84, -177.95) * mm});
            skPoint(sketch, "E274.visualSharp", {"position": v(-11.9, -146.78) * mm});
            skArc(sketch, "E274.filletArc", {"start": v(-5.85, -146.72) * mm, "mid": v(-9.72, -148.57) * mm, "end": v(-10.78, -152.73) * mm});
            skPoint(sketch, "E275.visualSharp", {"position": v(11.97, -146.52) * mm});
            skArc(sketch, "E275.filletArc", {"start": v(10.98, -152.5) * mm, "mid": v(9.83, -148.36) * mm, "end": v(5.91, -146.59) * mm});
            skPoint(sketch, "E276.endSnap0", {"position": v(0.03, -146.65) * mm});
            skLineSegment(sketch, "E277", {"start": v(39.74, -173.92) * mm, "end": v(35.5, -174.67) * mm});
            skLineSegment(sketch, "E278", {"start": v(29.87, -171.46) * mm, "end": v(22.97, -153.14) * mm});
            skLineSegment(sketch, "E279", {"start": v(43.94, -168.86) * mm, "end": v(43.73, -149.24) * mm});
            skLineSegment(sketch, "E280", {"start": v(37.71, -144.3) * mm, "end": v(26.79, -146.35) * mm});
            skPoint(sketch, "E281.visualSharp", {"position": v(43.99, -173.17) * mm});
            skArc(sketch, "E281.filletArc", {"start": v(39.74, -173.92) * mm, "mid": v(42.77, -172.16) * mm, "end": v(43.94, -168.86) * mm});
            skPoint(sketch, "E282.visualSharp", {"position": v(31.35, -175.4) * mm});
            skArc(sketch, "E282.filletArc", {"start": v(29.87, -171.46) * mm, "mid": v(32.1, -174.08) * mm, "end": v(35.5, -174.67) * mm});
            skPoint(sketch, "E283.visualSharp", {"position": v(20.84, -147.47) * mm});
            skArc(sketch, "E283.filletArc", {"start": v(26.79, -146.35) * mm, "mid": v(23.3, -148.86) * mm, "end": v(22.97, -153.14) * mm});
            skPoint(sketch, "E284.visualSharp", {"position": v(43.66, -143.19) * mm});
            skArc(sketch, "E284.filletArc", {"start": v(43.73, -149.24) * mm, "mid": v(41.87, -145.37) * mm, "end": v(37.71, -144.3) * mm});
            skPoint(sketch, "E285.endSnap0", {"position": v(32.25, -145.33) * mm});
            skLineSegment(sketch, "E286.MirrorCS", {"start": v(-37.99, -173.6) * mm, "end": v(-42.15, -172.48) * mm});
            skArc(sketch, "E287.MirrorCS", {"start": v(-45.9, -167.19) * mm, "mid": v(-44.98, -170.5) * mm, "end": v(-42.15, -172.48) * mm});
            skArc(sketch, "E288.MirrorCS", {"start": v(-37.99, -173.6) * mm, "mid": v(-34.5, -173.28) * mm, "end": v(-32.05, -170.78) * mm});
            skPoint(sketch, "E289.MirrorP", {"position": v(-32.7, -144.51) * mm});
            skPoint(sketch, "E290.MirrorP", {"position": v(-46.22, -171.39) * mm});
            skLineSegment(sketch, "E291.MirrorCS", {"start": v(-27.31, -145.9) * mm, "end": v(-38.08, -143.14) * mm});
            skArc(sketch, "E292.MirrorCS", {"start": v(-38.08, -143.14) * mm, "mid": v(-42.3, -143.93) * mm, "end": v(-44.4, -147.67) * mm});
            skArc(sketch, "E293.MirrorCS", {"start": v(-23.95, -152.91) * mm, "mid": v(-24, -148.62) * mm, "end": v(-27.31, -145.9) * mm});
            skPoint(sketch, "E294.MirrorP", {"position": v(-33.82, -174.7) * mm});
            skPoint(sketch, "E295.MirrorP", {"position": v(-21.45, -147.4) * mm});
            skLineSegment(sketch, "E296.MirrorCS", {"start": v(-32.05, -170.78) * mm, "end": v(-23.95, -152.91) * mm});
            skLineSegment(sketch, "E297.MirrorCS", {"start": v(-45.9, -167.19) * mm, "end": v(-44.4, -147.67) * mm});
            skLineSegment(sketch, "E298", {"start": v(177.8, 1.05) * mm, "end": v(177.6, -3.25) * mm});
            skLineSegment(sketch, "E299", {"start": v(173.23, -8.04) * mm, "end": v(153.84, -10.73) * mm});
            skLineSegment(sketch, "E300", {"start": v(173.8, 6.26) * mm, "end": v(154.61, 10.38) * mm});
            skLineSegment(sketch, "E301", {"start": v(148.47, 5.6) * mm, "end": v(148.06, -5.5) * mm});
            skPoint(sketch, "E302.visualSharp", {"position": v(178.01, 5.36) * mm});
            skArc(sketch, "E302.filletArc", {"start": v(177.8, 1.05) * mm, "mid": v(176.76, 4.4) * mm, "end": v(173.8, 6.26) * mm});
            skPoint(sketch, "E303.visualSharp", {"position": v(177.4, -7.46) * mm});
            skArc(sketch, "E303.filletArc", {"start": v(173.23, -8.04) * mm, "mid": v(176.28, -6.43) * mm, "end": v(177.6, -3.25) * mm});
            skPoint(sketch, "E304.visualSharp", {"position": v(147.84, -11.56) * mm});
            skArc(sketch, "E304.filletArc", {"start": v(148.06, -5.5) * mm, "mid": v(149.73, -9.46) * mm, "end": v(153.84, -10.73) * mm});
            skPoint(sketch, "E305.visualSharp", {"position": v(148.7, 11.65) * mm});
            skArc(sketch, "E305.filletArc", {"start": v(154.61, 10.38) * mm, "mid": v(150.43, 9.42) * mm, "end": v(148.47, 5.6) * mm});
            skPoint(sketch, "E306.endSnap0", {"position": v(148.27, 0.04) * mm});
            skArc(sketch, "E307.MirrorCS", {"start": v(-177.8, 1.05) * mm, "mid": v(-176.76, 4.4) * mm, "end": v(-173.8, 6.26) * mm});
            skPoint(sketch, "E308.MirrorP", {"position": v(-178.01, 5.36) * mm});
            skLineSegment(sketch, "E309.MirrorCS", {"start": v(-177.8, 1.05) * mm, "end": v(-177.6, -3.25) * mm});
            skPoint(sketch, "E310.MirrorP", {"position": v(-148.7, 11.65) * mm});
            skArc(sketch, "E311.MirrorCS", {"start": v(-154.61, 10.38) * mm, "mid": v(-150.43, 9.42) * mm, "end": v(-148.47, 5.6) * mm});
            skLineSegment(sketch, "E312.MirrorCS", {"start": v(-148.47, 5.6) * mm, "end": v(-148.06, -5.5) * mm});
            skLineSegment(sketch, "E313.MirrorCS", {"start": v(-173.8, 6.26) * mm, "end": v(-154.61, 10.38) * mm});
            skArc(sketch, "E314.MirrorCS", {"start": v(-173.23, -8.04) * mm, "mid": v(-176.28, -6.43) * mm, "end": v(-177.6, -3.25) * mm});
            skLineSegment(sketch, "E315.MirrorCS", {"start": v(-173.23, -8.04) * mm, "end": v(-153.84, -10.73) * mm});
            skPoint(sketch, "E316.MirrorP", {"position": v(-148.27, 0.04) * mm});
            skPoint(sketch, "E317.MirrorP", {"position": v(-147.84, -11.56) * mm});
            skPoint(sketch, "E318.MirrorP", {"position": v(-177.4, -7.46) * mm});
            skArc(sketch, "E319.MirrorCS", {"start": v(-148.06, -5.5) * mm, "mid": v(-149.73, -9.46) * mm, "end": v(-153.84, -10.73) * mm});
            skLineSegment(sketch, "E320", {"start": v(386.02, 129) * mm, "end": v(390.33, 129) * mm});
            skLineSegment(sketch, "E321", {"start": v(395.32, 124.85) * mm, "end": v(398.93, 105.61) * mm});
            skLineSegment(sketch, "E322", {"start": v(381.01, 124.74) * mm, "end": v(377.82, 105.38) * mm});
            skLineSegment(sketch, "E323", {"start": v(382.88, 99.48) * mm, "end": v(394, 99.6) * mm});
            skPoint(sketch, "E324.visualSharp", {"position": v(381.71, 129) * mm});
            skArc(sketch, "E324.filletArc", {"start": v(386.02, 129) * mm, "mid": v(382.74, 127.8) * mm, "end": v(381.01, 124.74) * mm});
            skPoint(sketch, "E325.visualSharp", {"position": v(394.55, 129) * mm});
            skArc(sketch, "E325.filletArc", {"start": v(395.32, 124.85) * mm, "mid": v(393.57, 127.83) * mm, "end": v(390.33, 129) * mm});
            skPoint(sketch, "E326.visualSharp", {"position": v(400.05, 99.66) * mm});
            skArc(sketch, "E326.filletArc", {"start": v(394, 99.6) * mm, "mid": v(397.87, 101.46) * mm, "end": v(398.93, 105.61) * mm});
            skPoint(sketch, "E327.visualSharp", {"position": v(376.83, 99.41) * mm});
            skArc(sketch, "E327.filletArc", {"start": v(377.82, 105.38) * mm, "mid": v(378.97, 101.25) * mm, "end": v(382.88, 99.48) * mm});
            skPoint(sketch, "E328.endSnap0", {"position": v(388.44, 99.54) * mm});
            skLineSegment(sketch, "E329", {"start": v(-2.55, 177.46) * mm, "end": v(1.75, 177.46) * mm});
            skLineSegment(sketch, "E330", {"start": v(6.75, 173.31) * mm, "end": v(10.36, 154.07) * mm});
            skLineSegment(sketch, "E331", {"start": v(-7.56, 173.2) * mm, "end": v(-10.76, 153.84) * mm});
            skLineSegment(sketch, "E332", {"start": v(-5.7, 147.94) * mm, "end": v(5.42, 148.06) * mm});
            skPoint(sketch, "E333.visualSharp", {"position": v(-6.86, 177.46) * mm});
            skArc(sketch, "E333.filletArc", {"start": v(-2.55, 177.46) * mm, "mid": v(-5.84, 176.25) * mm, "end": v(-7.56, 173.2) * mm});
            skPoint(sketch, "E334.visualSharp", {"position": v(5.97, 177.46) * mm});
            skArc(sketch, "E334.filletArc", {"start": v(6.75, 173.31) * mm, "mid": v(5, 176.28) * mm, "end": v(1.75, 177.46) * mm});
            skPoint(sketch, "E335.visualSharp", {"position": v(11.47, 148.12) * mm});
            skArc(sketch, "E335.filletArc", {"start": v(5.42, 148.06) * mm, "mid": v(9.29, 149.91) * mm, "end": v(10.36, 154.07) * mm});
            skPoint(sketch, "E336.visualSharp", {"position": v(-11.75, 147.87) * mm});
            skArc(sketch, "E336.filletArc", {"start": v(-10.76, 153.84) * mm, "mid": v(-9.6, 149.7) * mm, "end": v(-5.7, 147.94) * mm});
            skPoint(sketch, "E337.endSnap0", {"position": v(-0.14, 148) * mm});
            skLineSegment(sketch, "E338", {"start": v(312.07, 28.72) * mm, "end": v(464.47, 28.72) * mm});
            skLineSegment(sketch, "E339", {"start": v(388.27, -47.48) * mm, "end": v(388.44, 104.92) * mm});
            skLineSegment(sketch, "E340.MirrorCS", {"start": v(386.02, -71.55) * mm, "end": v(390.33, -71.55) * mm});
            skLineSegment(sketch, "E341.MirrorCS", {"start": v(382.88, -42.03) * mm, "end": v(394, -42.15) * mm});
            skArc(sketch, "E342.MirrorCS", {"start": v(386.02, -71.55) * mm, "mid": v(382.74, -70.34) * mm, "end": v(381.01, -67.3) * mm});
            skArc(sketch, "E343.MirrorCS", {"start": v(394, -42.15) * mm, "mid": v(397.87, -44) * mm, "end": v(398.93, -48.17) * mm});
            skArc(sketch, "E344.MirrorCS", {"start": v(395.32, -67.4) * mm, "mid": v(393.57, -70.38) * mm, "end": v(390.33, -71.55) * mm});
            skArc(sketch, "E345.MirrorCS", {"start": v(377.82, -47.94) * mm, "mid": v(378.97, -43.8) * mm, "end": v(382.88, -42.03) * mm});
            skLineSegment(sketch, "E346.MirrorCS", {"start": v(381.01, -67.3) * mm, "end": v(377.82, -47.94) * mm});
            skLineSegment(sketch, "E347.MirrorCS", {"start": v(395.32, -67.4) * mm, "end": v(398.93, -48.17) * mm});
            skPoint(sketch, "E348.MirrorP", {"position": v(388.44, -42.1) * mm});
            skPoint(sketch, "E349.MirrorP", {"position": v(376.83, -41.96) * mm});
            skPoint(sketch, "E350.MirrorP", {"position": v(400.05, -42.22) * mm});
            skPoint(sketch, "E351.MirrorP", {"position": v(394.55, -71.55) * mm});
            skPoint(sketch, "E352.MirrorP", {"position": v(381.71, -71.55) * mm});
            skLineSegment(sketch, "E353", {"start": v(488.84, 28.62) * mm, "end": v(488.67, 24.31) * mm});
            skLineSegment(sketch, "E354", {"start": v(484.35, 19.48) * mm, "end": v(464.99, 16.6) * mm});
            skLineSegment(sketch, "E355", {"start": v(484.78, 33.78) * mm, "end": v(465.55, 37.7) * mm});
            skLineSegment(sketch, "E356", {"start": v(459.46, 32.87) * mm, "end": v(459.16, 21.76) * mm});
            skPoint(sketch, "E357.visualSharp", {"position": v(489, 32.92) * mm});
            skArc(sketch, "E357.filletArc", {"start": v(488.84, 28.62) * mm, "mid": v(487.76, 31.95) * mm, "end": v(484.78, 33.78) * mm});
            skPoint(sketch, "E358.visualSharp", {"position": v(488.52, 20.1) * mm});
            skArc(sketch, "E358.filletArc", {"start": v(484.35, 19.48) * mm, "mid": v(487.38, 21.11) * mm, "end": v(488.67, 24.31) * mm});
            skPoint(sketch, "E359.visualSharp", {"position": v(459, 15.7) * mm});
            skArc(sketch, "E359.filletArc", {"start": v(459.16, 21.76) * mm, "mid": v(460.87, 17.82) * mm, "end": v(464.99, 16.6) * mm});
            skPoint(sketch, "E360.visualSharp", {"position": v(459.62, 38.92) * mm});
            skArc(sketch, "E360.filletArc", {"start": v(465.55, 37.7) * mm, "mid": v(461.38, 36.7) * mm, "end": v(459.46, 32.87) * mm});
            skPoint(sketch, "E361.endSnap0", {"position": v(459.3, 27.31) * mm});
            skLineSegment(sketch, "E362", {"start": v(294.84, 65.27) * mm, "end": v(296.47, 69.25) * mm});
            skLineSegment(sketch, "E363", {"start": v(302.2, 72.3) * mm, "end": v(321.37, 68.32) * mm});
            skLineSegment(sketch, "E364", {"start": v(296.87, 59.02) * mm, "end": v(313.56, 48.7) * mm});
            skLineSegment(sketch, "E365", {"start": v(320.95, 51.14) * mm, "end": v(325.06, 61.47) * mm});
            skPoint(sketch, "E366.visualSharp", {"position": v(293.2, 61.28) * mm});
            skArc(sketch, "E366.filletArc", {"start": v(294.84, 65.27) * mm, "mid": v(294.7, 61.77) * mm, "end": v(296.87, 59.02) * mm});
            skPoint(sketch, "E367.visualSharp", {"position": v(298.08, 73.15) * mm});
            skArc(sketch, "E367.filletArc", {"start": v(302.2, 72.3) * mm, "mid": v(298.8, 71.8) * mm, "end": v(296.47, 69.25) * mm});
            skPoint(sketch, "E368.visualSharp", {"position": v(327.3, 67.1) * mm});
            skArc(sketch, "E368.filletArc", {"start": v(325.06, 61.47) * mm, "mid": v(324.81, 65.75) * mm, "end": v(321.37, 68.32) * mm});
            skPoint(sketch, "E369.visualSharp", {"position": v(318.7, 45.52) * mm});
            skArc(sketch, "E369.filletArc", {"start": v(313.56, 48.7) * mm, "mid": v(317.82, 48.2) * mm, "end": v(320.95, 51.14) * mm});
            skPoint(sketch, "E370.endSnap0", {"position": v(323, 56.3) * mm});
            skLineSegment(sketch, "E371", {"start": v(287.74, 27.2) * mm, "end": v(287.86, 31.5) * mm});
            skLineSegment(sketch, "E372", {"start": v(292.15, 36.38) * mm, "end": v(311.48, 39.43) * mm});
            skLineSegment(sketch, "E373", {"start": v(291.84, 22.07) * mm, "end": v(311.1, 18.32) * mm});
            skLineSegment(sketch, "E374", {"start": v(317.15, 23.21) * mm, "end": v(317.35, 34.32) * mm});
            skPoint(sketch, "E375.visualSharp", {"position": v(287.61, 22.9) * mm});
            skArc(sketch, "E375.filletArc", {"start": v(287.74, 27.2) * mm, "mid": v(288.85, 23.88) * mm, "end": v(291.84, 22.07) * mm});
            skPoint(sketch, "E376.visualSharp", {"position": v(287.98, 35.72) * mm});
            skArc(sketch, "E376.filletArc", {"start": v(292.15, 36.38) * mm, "mid": v(289.13, 34.71) * mm, "end": v(287.86, 31.5) * mm});
            skPoint(sketch, "E377.visualSharp", {"position": v(317.46, 40.38) * mm});
            skArc(sketch, "E377.filletArc", {"start": v(317.35, 34.32) * mm, "mid": v(315.6, 38.25) * mm, "end": v(311.48, 39.43) * mm});
            skPoint(sketch, "E378.visualSharp", {"position": v(317.05, 17.16) * mm});
            skArc(sketch, "E378.filletArc", {"start": v(311.1, 18.32) * mm, "mid": v(315.27, 19.35) * mm, "end": v(317.15, 23.21) * mm});
            skPoint(sketch, "E379.endSnap0", {"position": v(317.25, 28.77) * mm});
            skLineSegment(sketch, "E380", {"start": v(315.17, 97.45) * mm, "end": v(318.19, 100.52) * mm});
            skLineSegment(sketch, "E381", {"start": v(324.64, 101.18) * mm, "end": v(340.9, 90.27) * mm});
            skLineSegment(sketch, "E382", {"start": v(314.7, 90.9) * mm, "end": v(326.27, 75.05) * mm});
            skLineSegment(sketch, "E383", {"start": v(334.03, 74.52) * mm, "end": v(341.73, 82.54) * mm});
            skPoint(sketch, "E384.visualSharp", {"position": v(312.15, 94.37) * mm});
            skArc(sketch, "E384.filletArc", {"start": v(315.17, 97.45) * mm, "mid": v(313.73, 94.26) * mm, "end": v(314.7, 90.9) * mm});
            skPoint(sketch, "E385.visualSharp", {"position": v(321.14, 103.53) * mm});
            skArc(sketch, "E385.filletArc", {"start": v(324.64, 101.18) * mm, "mid": v(321.3, 102.01) * mm, "end": v(318.19, 100.52) * mm});
            skPoint(sketch, "E386.visualSharp", {"position": v(345.93, 86.9) * mm});
            skArc(sketch, "E386.filletArc", {"start": v(341.73, 82.54) * mm, "mid": v(343.12, 86.6) * mm, "end": v(340.9, 90.27) * mm});
            skPoint(sketch, "E387.visualSharp", {"position": v(329.84, 70.16) * mm});
            skArc(sketch, "E387.filletArc", {"start": v(326.27, 75.05) * mm, "mid": v(330.03, 72.97) * mm, "end": v(334.03, 74.52) * mm});
            skPoint(sketch, "E388.endSnap0", {"position": v(337.88, 78.53) * mm});
            skLineSegment(sketch, "E389", {"start": v(345.96, 119.63) * mm, "end": v(349.85, 121.5) * mm});
            skLineSegment(sketch, "E390", {"start": v(356.14, 119.91) * mm, "end": v(367.7, 104.12) * mm});
            skLineSegment(sketch, "E391", {"start": v(343.28, 113.63) * mm, "end": v(348.76, 94.8) * mm});
            skLineSegment(sketch, "E392", {"start": v(355.88, 91.65) * mm, "end": v(365.85, 96.56) * mm});
            skPoint(sketch, "E393.visualSharp", {"position": v(342.08, 117.77) * mm});
            skArc(sketch, "E393.filletArc", {"start": v(345.96, 119.63) * mm, "mid": v(343.52, 117.12) * mm, "end": v(343.28, 113.63) * mm});
            skPoint(sketch, "E394.visualSharp", {"position": v(353.65, 123.31) * mm});
            skArc(sketch, "E394.filletArc", {"start": v(356.14, 119.91) * mm, "mid": v(353.28, 121.84) * mm, "end": v(349.85, 121.5) * mm});
            skPoint(sketch, "E395.visualSharp", {"position": v(371.28, 99.24) * mm});
            skArc(sketch, "E395.filletArc", {"start": v(365.85, 96.56) * mm, "mid": v(368.54, 99.9) * mm, "end": v(367.7, 104.12) * mm});
            skPoint(sketch, "E396.visualSharp", {"position": v(350.45, 88.98) * mm});
            skArc(sketch, "E396.filletArc", {"start": v(348.76, 94.8) * mm, "mid": v(351.6, 91.56) * mm, "end": v(355.88, 91.65) * mm});
            skPoint(sketch, "E397.endSnap0", {"position": v(360.87, 94.1) * mm});
            skLineSegment(sketch, "E398.MirrorCS", {"start": v(430.95, 119.54) * mm, "end": v(427.07, 121.4) * mm});
            skLineSegment(sketch, "E399.MirrorCS", {"start": v(461.7, 97.29) * mm, "end": v(458.68, 100.37) * mm});
            skLineSegment(sketch, "E400.MirrorCS", {"start": v(481.95, 65.07) * mm, "end": v(480.33, 69.05) * mm});
            skArc(sketch, "E401.MirrorCS", {"start": v(463.2, 48.54) * mm, "mid": v(458.93, 48.05) * mm, "end": v(455.81, 51) * mm});
            skArc(sketch, "E402.MirrorCS", {"start": v(451.73, 61.33) * mm, "mid": v(451.98, 65.62) * mm, "end": v(455.43, 68.18) * mm});
            skArc(sketch, "E403.MirrorCS", {"start": v(450.54, 74.91) * mm, "mid": v(446.78, 72.85) * mm, "end": v(442.78, 74.4) * mm});
            skArc(sketch, "E404.MirrorCS", {"start": v(481.95, 65.07) * mm, "mid": v(482.08, 61.57) * mm, "end": v(479.91, 58.82) * mm});
            skLineSegment(sketch, "E405.MirrorCS", {"start": v(420.97, 91.58) * mm, "end": v(411, 96.51) * mm});
            skArc(sketch, "E406.MirrorCS", {"start": v(430.95, 119.54) * mm, "mid": v(433.38, 117.03) * mm, "end": v(433.62, 113.53) * mm});
            skArc(sketch, "E407.MirrorCS", {"start": v(420.77, 119.84) * mm, "mid": v(423.64, 121.76) * mm, "end": v(427.07, 121.4) * mm});
            skArc(sketch, "E408.MirrorCS", {"start": v(461.7, 97.29) * mm, "mid": v(463.13, 94.1) * mm, "end": v(462.15, 90.73) * mm});
            skArc(sketch, "E409.MirrorCS", {"start": v(411, 96.51) * mm, "mid": v(408.33, 99.87) * mm, "end": v(409.17, 104.08) * mm});
            skArc(sketch, "E410.MirrorCS", {"start": v(428.1, 94.7) * mm, "mid": v(425.26, 91.48) * mm, "end": v(420.97, 91.58) * mm});
            skLineSegment(sketch, "E411.MirrorCS", {"start": v(455.81, 51) * mm, "end": v(451.73, 61.33) * mm});
            skArc(sketch, "E412.MirrorCS", {"start": v(474.6, 72.1) * mm, "mid": v(478.02, 71.61) * mm, "end": v(480.33, 69.05) * mm});
            skArc(sketch, "E413.MirrorCS", {"start": v(452.23, 101.04) * mm, "mid": v(455.57, 101.87) * mm, "end": v(458.68, 100.37) * mm});
            skLineSegment(sketch, "E414.MirrorCS", {"start": v(442.78, 74.4) * mm, "end": v(435.1, 82.43) * mm});
            skArc(sketch, "E415.MirrorCS", {"start": v(435.1, 82.43) * mm, "mid": v(433.72, 86.5) * mm, "end": v(435.95, 90.17) * mm});
            skPoint(sketch, "E416.MirrorP", {"position": v(423.27, 123.24) * mm});
            skPoint(sketch, "E417.MirrorP", {"position": v(438.94, 78.42) * mm});
            skPoint(sketch, "E418.MirrorP", {"position": v(405.58, 99.2) * mm});
            skLineSegment(sketch, "E419.MirrorCS", {"start": v(420.77, 119.84) * mm, "end": v(409.17, 104.08) * mm});
            skPoint(sketch, "E420.MirrorP", {"position": v(483.58, 61.08) * mm});
            skLineSegment(sketch, "E421.MirrorCS", {"start": v(433.62, 113.53) * mm, "end": v(428.1, 94.7) * mm});
            skPoint(sketch, "E422.MirrorP", {"position": v(426.4, 88.9) * mm});
            skPoint(sketch, "E423.MirrorP", {"position": v(464.7, 94.2) * mm});
            skPoint(sketch, "E424.MirrorP", {"position": v(478.73, 72.96) * mm});
            skPoint(sketch, "E425.MirrorP", {"position": v(415.99, 94.05) * mm});
            skLineSegment(sketch, "E426.MirrorCS", {"start": v(462.15, 90.73) * mm, "end": v(450.54, 74.91) * mm});
            skPoint(sketch, "E427.MirrorP", {"position": v(455.73, 103.38) * mm});
            skPoint(sketch, "E428.MirrorP", {"position": v(449.5, 66.96) * mm});
            skLineSegment(sketch, "E429.MirrorCS", {"start": v(479.91, 58.82) * mm, "end": v(463.2, 48.54) * mm});
            skPoint(sketch, "E430.MirrorP", {"position": v(430.91, 86.8) * mm});
            skPoint(sketch, "E431.MirrorP", {"position": v(458.04, 45.37) * mm});
            skLineSegment(sketch, "E432.MirrorCS", {"start": v(474.6, 72.1) * mm, "end": v(455.43, 68.18) * mm});
            skPoint(sketch, "E433.MirrorP", {"position": v(434.83, 117.67) * mm});
            skPoint(sketch, "E434.MirrorP", {"position": v(446.96, 70.03) * mm});
            skPoint(sketch, "E435.MirrorP", {"position": v(453.77, 56.16) * mm});
            skLineSegment(sketch, "E436.MirrorCS", {"start": v(452.23, 101.04) * mm, "end": v(435.95, 90.17) * mm});
            skLineSegment(sketch, "E437.MirrorCS", {"start": v(294.84, -7.82) * mm, "end": v(296.47, -11.8) * mm});
            skLineSegment(sketch, "E438.MirrorCS", {"start": v(315.17, -40) * mm, "end": v(318.19, -43.07) * mm});
            skLineSegment(sketch, "E439.MirrorCS", {"start": v(345.96, -62.18) * mm, "end": v(349.85, -64.04) * mm});
            skArc(sketch, "E440.MirrorCS", {"start": v(294.84, -7.82) * mm, "mid": v(294.7, -4.32) * mm, "end": v(296.87, -1.57) * mm});
            skArc(sketch, "E441.MirrorCS", {"start": v(356.14, -62.46) * mm, "mid": v(353.28, -64.39) * mm, "end": v(349.85, -64.04) * mm});
            skArc(sketch, "E442.MirrorCS", {"start": v(345.96, -62.18) * mm, "mid": v(343.52, -59.68) * mm, "end": v(343.28, -56.18) * mm});
            skLineSegment(sketch, "E443.MirrorCS", {"start": v(355.88, -34.2) * mm, "end": v(365.85, -39.11) * mm});
            skLineSegment(sketch, "E444.MirrorCS", {"start": v(320.95, 6.3) * mm, "end": v(325.06, -4.02) * mm});
            skLineSegment(sketch, "E445.MirrorCS", {"start": v(334.03, -17.08) * mm, "end": v(341.73, -25.09) * mm});
            skArc(sketch, "E446.MirrorCS", {"start": v(315.17, -40) * mm, "mid": v(313.73, -36.8) * mm, "end": v(314.7, -33.44) * mm});
            skArc(sketch, "E447.MirrorCS", {"start": v(324.64, -43.73) * mm, "mid": v(321.3, -44.57) * mm, "end": v(318.19, -43.07) * mm});
            skArc(sketch, "E448.MirrorCS", {"start": v(302.2, -14.85) * mm, "mid": v(298.8, -14.36) * mm, "end": v(296.47, -11.8) * mm});
            skPoint(sketch, "E449.MirrorP", {"position": v(329.84, -12.7) * mm});
            skPoint(sketch, "E450.MirrorP", {"position": v(323, 1.14) * mm});
            skLineSegment(sketch, "E451.MirrorCS", {"start": v(356.14, -62.46) * mm, "end": v(367.7, -46.67) * mm});
            skArc(sketch, "E452.MirrorCS", {"start": v(325.06, -4.02) * mm, "mid": v(324.81, -8.3) * mm, "end": v(321.37, -10.87) * mm});
            skLineSegment(sketch, "E453.MirrorCS", {"start": v(302.2, -14.85) * mm, "end": v(321.37, -10.87) * mm});
            skLineSegment(sketch, "E454.MirrorCS", {"start": v(324.64, -43.73) * mm, "end": v(340.9, -32.83) * mm});
            skPoint(sketch, "E455.MirrorP", {"position": v(318.7, 11.93) * mm});
            skPoint(sketch, "E456.MirrorP", {"position": v(345.93, -29.45) * mm});
            skArc(sketch, "E457.MirrorCS", {"start": v(348.76, -37.34) * mm, "mid": v(351.6, -34.11) * mm, "end": v(355.88, -34.2) * mm});
            skArc(sketch, "E458.MirrorCS", {"start": v(365.85, -39.11) * mm, "mid": v(368.54, -42.46) * mm, "end": v(367.7, -46.67) * mm});
            skArc(sketch, "E459.MirrorCS", {"start": v(341.73, -25.09) * mm, "mid": v(343.12, -29.15) * mm, "end": v(340.9, -32.83) * mm});
            skPoint(sketch, "E460.MirrorP", {"position": v(327.3, -9.64) * mm});
            skPoint(sketch, "E461.MirrorP", {"position": v(321.14, -46.08) * mm});
            skPoint(sketch, "E462.MirrorP", {"position": v(360.87, -36.66) * mm});
            skPoint(sketch, "E463.MirrorP", {"position": v(312.15, -36.92) * mm});
            skPoint(sketch, "E464.MirrorP", {"position": v(298.08, -15.7) * mm});
            skArc(sketch, "E465.MirrorCS", {"start": v(326.27, -17.6) * mm, "mid": v(330.03, -15.53) * mm, "end": v(334.03, -17.08) * mm});
            skPoint(sketch, "E466.MirrorP", {"position": v(350.45, -31.53) * mm});
            skArc(sketch, "E467.MirrorCS", {"start": v(313.56, 8.75) * mm, "mid": v(317.82, 9.25) * mm, "end": v(320.95, 6.3) * mm});
            skLineSegment(sketch, "E468.MirrorCS", {"start": v(343.28, -56.18) * mm, "end": v(348.76, -37.34) * mm});
            skPoint(sketch, "E469.MirrorP", {"position": v(293.2, -3.84) * mm});
            skLineSegment(sketch, "E470.MirrorCS", {"start": v(314.7, -33.44) * mm, "end": v(326.27, -17.6) * mm});
            skLineSegment(sketch, "E471.MirrorCS", {"start": v(296.87, -1.57) * mm, "end": v(313.56, 8.75) * mm});
            skPoint(sketch, "E472.MirrorP", {"position": v(371.28, -41.79) * mm});
            skPoint(sketch, "E473.MirrorP", {"position": v(353.65, -65.87) * mm});
            skPoint(sketch, "E474.MirrorP", {"position": v(337.88, -21.08) * mm});
            skPoint(sketch, "E475.MirrorP", {"position": v(342.08, -60.32) * mm});
            skLineSegment(sketch, "E476.MirrorCS", {"start": v(430.95, -62.1) * mm, "end": v(427.07, -63.96) * mm});
            skLineSegment(sketch, "E477.MirrorCS", {"start": v(461.7, -39.84) * mm, "end": v(458.68, -42.92) * mm});
            skLineSegment(sketch, "E478.MirrorCS", {"start": v(481.95, -7.62) * mm, "end": v(480.33, -11.6) * mm});
            skArc(sketch, "E479.MirrorCS", {"start": v(481.95, -7.62) * mm, "mid": v(482.08, -4.12) * mm, "end": v(479.91, -1.37) * mm});
            skArc(sketch, "E480.MirrorCS", {"start": v(451.73, -3.88) * mm, "mid": v(451.98, -8.17) * mm, "end": v(455.43, -10.73) * mm});
            skLineSegment(sketch, "E481.MirrorCS", {"start": v(420.97, -34.13) * mm, "end": v(411, -39.07) * mm});
            skArc(sketch, "E482.MirrorCS", {"start": v(430.95, -62.1) * mm, "mid": v(433.38, -59.58) * mm, "end": v(433.62, -56.08) * mm});
            skArc(sketch, "E483.MirrorCS", {"start": v(420.77, -62.4) * mm, "mid": v(423.64, -64.31) * mm, "end": v(427.07, -63.96) * mm});
            skArc(sketch, "E484.MirrorCS", {"start": v(461.7, -39.84) * mm, "mid": v(463.13, -36.65) * mm, "end": v(462.15, -33.28) * mm});
            skLineSegment(sketch, "E485.MirrorCS", {"start": v(442.78, -16.96) * mm, "end": v(435.1, -24.99) * mm});
            skArc(sketch, "E486.MirrorCS", {"start": v(411, -39.07) * mm, "mid": v(408.33, -42.42) * mm, "end": v(409.17, -46.63) * mm});
            skArc(sketch, "E487.MirrorCS", {"start": v(428.1, -37.26) * mm, "mid": v(425.26, -34.03) * mm, "end": v(420.97, -34.13) * mm});
            skLineSegment(sketch, "E488.MirrorCS", {"start": v(455.81, 6.45) * mm, "end": v(451.73, -3.88) * mm});
            skArc(sketch, "E489.MirrorCS", {"start": v(474.6, -14.66) * mm, "mid": v(478.02, -14.17) * mm, "end": v(480.33, -11.6) * mm});
            skArc(sketch, "E490.MirrorCS", {"start": v(463.2, 8.9) * mm, "mid": v(458.93, 9.4) * mm, "end": v(455.81, 6.45) * mm});
            skArc(sketch, "E491.MirrorCS", {"start": v(450.54, -17.46) * mm, "mid": v(446.78, -15.4) * mm, "end": v(442.78, -16.96) * mm});
            skArc(sketch, "E492.MirrorCS", {"start": v(435.1, -24.99) * mm, "mid": v(433.72, -29.05) * mm, "end": v(435.95, -32.72) * mm});
            skArc(sketch, "E493.MirrorCS", {"start": v(452.23, -43.6) * mm, "mid": v(455.57, -44.42) * mm, "end": v(458.68, -42.92) * mm});
            skLineSegment(sketch, "E494.MirrorCS", {"start": v(474.6, -14.66) * mm, "end": v(455.43, -10.73) * mm});
            skLineSegment(sketch, "E495.MirrorCS", {"start": v(462.15, -33.28) * mm, "end": v(450.54, -17.46) * mm});
            skPoint(sketch, "E496.MirrorP", {"position": v(434.83, -60.22) * mm});
            skLineSegment(sketch, "E497.MirrorCS", {"start": v(452.23, -43.6) * mm, "end": v(435.95, -32.72) * mm});
            skPoint(sketch, "E498.MirrorP", {"position": v(415.99, -36.6) * mm});
            skPoint(sketch, "E499.MirrorP", {"position": v(446.96, -12.58) * mm});
            skPoint(sketch, "E500.MirrorP", {"position": v(423.27, -65.79) * mm});
            skPoint(sketch, "E501.MirrorP", {"position": v(438.94, -20.97) * mm});
            skPoint(sketch, "E502.MirrorP", {"position": v(405.58, -41.75) * mm});
            skPoint(sketch, "E503.MirrorP", {"position": v(483.58, -3.63) * mm});
            skPoint(sketch, "E504.MirrorP", {"position": v(458.04, 12.08) * mm});
            skLineSegment(sketch, "E505.MirrorCS", {"start": v(433.62, -56.08) * mm, "end": v(428.1, -37.26) * mm});
            skPoint(sketch, "E506.MirrorP", {"position": v(426.4, -31.45) * mm});
            skPoint(sketch, "E507.MirrorP", {"position": v(449.5, -9.51) * mm});
            skPoint(sketch, "E508.MirrorP", {"position": v(464.7, -36.76) * mm});
            skLineSegment(sketch, "E509.MirrorCS", {"start": v(420.77, -62.4) * mm, "end": v(409.17, -46.63) * mm});
            skLineSegment(sketch, "E510.MirrorCS", {"start": v(479.91, -1.37) * mm, "end": v(463.2, 8.9) * mm});
            skPoint(sketch, "E511.MirrorP", {"position": v(430.91, -29.36) * mm});
            skPoint(sketch, "E512.MirrorP", {"position": v(478.73, -15.5) * mm});
            skPoint(sketch, "E513.MirrorP", {"position": v(455.73, -45.93) * mm});
            skPoint(sketch, "E514.MirrorP", {"position": v(453.77, 1.28) * mm});
            skCircle(sketch, "E515", {"center": v(-276.82, 25.9) * mm, "radius": 6.35 * mm});
            skCircle(sketch, "E516", {"center": v(-276.82, 25.9) * mm, "radius": 76.2 * mm});
            skLineSegment(sketch, "E517", {"start": v(-279.07, 126.18) * mm, "end": v(-274.77, 126.18) * mm});
            skLineSegment(sketch, "E518", {"start": v(-269.77, 122.03) * mm, "end": v(-266.17, 102.8) * mm});
            skLineSegment(sketch, "E519", {"start": v(-284.09, 121.92) * mm, "end": v(-287.28, 102.57) * mm});
            skLineSegment(sketch, "E520", {"start": v(-282.21, 96.66) * mm, "end": v(-271.1, 96.78) * mm});
            skPoint(sketch, "E521.visualSharp", {"position": v(-283.38, 126.18) * mm});
            skArc(sketch, "E521.filletArc", {"start": v(-279.07, 126.18) * mm, "mid": v(-282.36, 124.97) * mm, "end": v(-284.09, 121.92) * mm});
            skPoint(sketch, "E522.visualSharp", {"position": v(-270.55, 126.18) * mm});
            skArc(sketch, "E522.filletArc", {"start": v(-269.77, 122.03) * mm, "mid": v(-271.52, 125) * mm, "end": v(-274.77, 126.18) * mm});
            skPoint(sketch, "E523.visualSharp", {"position": v(-265.05, 96.85) * mm});
            skArc(sketch, "E523.filletArc", {"start": v(-271.1, 96.78) * mm, "mid": v(-267.23, 98.64) * mm, "end": v(-266.17, 102.8) * mm});
            skPoint(sketch, "E524.visualSharp", {"position": v(-288.27, 96.6) * mm});
            skArc(sketch, "E524.filletArc", {"start": v(-287.28, 102.57) * mm, "mid": v(-286.13, 98.43) * mm, "end": v(-282.21, 96.66) * mm});
            skPoint(sketch, "E525.endSnap0", {"position": v(-276.66, 96.72) * mm});
            skLineSegment(sketch, "E526", {"start": v(-353.02, 25.9) * mm, "end": v(-200.62, 25.9) * mm});
            skLineSegment(sketch, "E527", {"start": v(-276.82, -50.3) * mm, "end": v(-276.66, 102.1) * mm});
            skLineSegment(sketch, "E528.MirrorCS", {"start": v(-279.07, -74.37) * mm, "end": v(-274.77, -74.37) * mm});
            skLineSegment(sketch, "E529.MirrorCS", {"start": v(-282.21, -44.85) * mm, "end": v(-271.1, -44.97) * mm});
            skArc(sketch, "E530.MirrorCS", {"start": v(-279.07, -74.37) * mm, "mid": v(-282.36, -73.16) * mm, "end": v(-284.09, -70.12) * mm});
            skArc(sketch, "E531.MirrorCS", {"start": v(-271.1, -44.97) * mm, "mid": v(-267.23, -46.83) * mm, "end": v(-266.17, -50.99) * mm});
            skArc(sketch, "E532.MirrorCS", {"start": v(-269.77, -70.22) * mm, "mid": v(-271.52, -73.2) * mm, "end": v(-274.77, -74.37) * mm});
            skArc(sketch, "E533.MirrorCS", {"start": v(-287.28, -50.76) * mm, "mid": v(-286.13, -46.62) * mm, "end": v(-282.21, -44.85) * mm});
            skLineSegment(sketch, "E534.MirrorCS", {"start": v(-284.09, -70.12) * mm, "end": v(-287.28, -50.76) * mm});
            skLineSegment(sketch, "E535.MirrorCS", {"start": v(-269.77, -70.22) * mm, "end": v(-266.17, -50.99) * mm});
            skPoint(sketch, "E536.MirrorP", {"position": v(-276.66, -44.9) * mm});
            skPoint(sketch, "E537.MirrorP", {"position": v(-288.27, -44.78) * mm});
            skPoint(sketch, "E538.MirrorP", {"position": v(-265.05, -45.04) * mm});
            skPoint(sketch, "E539.MirrorP", {"position": v(-270.55, -74.37) * mm});
            skPoint(sketch, "E540.MirrorP", {"position": v(-283.38, -74.37) * mm});
            skLineSegment(sketch, "E541", {"start": v(-176.29, 25.16) * mm, "end": v(-176.42, 21.5) * mm});
            skLineSegment(sketch, "E542", {"start": v(-180.75, 16.66) * mm, "end": v(-200.11, 13.78) * mm});
            skLineSegment(sketch, "E543", {"start": v(-180.35, 30.33) * mm, "end": v(-199.56, 34.25) * mm});
            skLineSegment(sketch, "E544", {"start": v(-205.66, 29.4) * mm, "end": v(-205.94, 18.94) * mm});
            skPoint(sketch, "E545.visualSharp", {"position": v(-176.12, 29.47) * mm});
            skArc(sketch, "E545.filletArc", {"start": v(-176.29, 25.16) * mm, "mid": v(-177.37, 28.49) * mm, "end": v(-180.35, 30.33) * mm});
            skPoint(sketch, "E546.visualSharp", {"position": v(-176.58, 17.28) * mm});
            skArc(sketch, "E546.filletArc", {"start": v(-180.75, 16.66) * mm, "mid": v(-177.72, 18.3) * mm, "end": v(-176.42, 21.5) * mm});
            skPoint(sketch, "E547.visualSharp", {"position": v(-206.1, 12.89) * mm});
            skArc(sketch, "E547.filletArc", {"start": v(-205.94, 18.94) * mm, "mid": v(-204.23, 15) * mm, "end": v(-200.11, 13.78) * mm});
            skPoint(sketch, "E548.visualSharp", {"position": v(-205.5, 35.46) * mm});
            skArc(sketch, "E548.filletArc", {"start": v(-199.56, 34.25) * mm, "mid": v(-203.74, 33.25) * mm, "end": v(-205.66, 29.4) * mm});
            skPoint(sketch, "E549.endSnap0", {"position": v(-205.8, 24.17) * mm});
            skLineSegment(sketch, "E550", {"start": v(-370.26, 62.45) * mm, "end": v(-368.62, 66.43) * mm});
            skLineSegment(sketch, "E551", {"start": v(-362.9, 69.48) * mm, "end": v(-343.73, 65.5) * mm});
            skLineSegment(sketch, "E552", {"start": v(-368.23, 56.2) * mm, "end": v(-351.54, 45.88) * mm});
            skLineSegment(sketch, "E553", {"start": v(-344.15, 48.32) * mm, "end": v(-340.04, 58.65) * mm});
            skPoint(sketch, "E554.visualSharp", {"position": v(-371.9, 58.46) * mm});
            skArc(sketch, "E554.filletArc", {"start": v(-370.26, 62.45) * mm, "mid": v(-370.4, 58.95) * mm, "end": v(-368.23, 56.2) * mm});
            skPoint(sketch, "E555.visualSharp", {"position": v(-367.02, 70.33) * mm});
            skArc(sketch, "E555.filletArc", {"start": v(-362.9, 69.48) * mm, "mid": v(-366.3, 68.99) * mm, "end": v(-368.62, 66.43) * mm});
            skPoint(sketch, "E556.visualSharp", {"position": v(-337.8, 64.27) * mm});
            skArc(sketch, "E556.filletArc", {"start": v(-340.04, 58.65) * mm, "mid": v(-340.29, 62.93) * mm, "end": v(-343.73, 65.5) * mm});
            skPoint(sketch, "E557.visualSharp", {"position": v(-346.4, 42.7) * mm});
            skArc(sketch, "E557.filletArc", {"start": v(-351.54, 45.88) * mm, "mid": v(-347.28, 45.38) * mm, "end": v(-344.15, 48.32) * mm});
            skPoint(sketch, "E558.endSnap0", {"position": v(-342.1, 53.49) * mm});
            skLineSegment(sketch, "E559", {"start": v(-377.36, 24.38) * mm, "end": v(-377.24, 28.69) * mm});
            skLineSegment(sketch, "E560", {"start": v(-372.95, 33.56) * mm, "end": v(-353.62, 36.61) * mm});
            skLineSegment(sketch, "E561", {"start": v(-373.25, 19.25) * mm, "end": v(-354, 15.5) * mm});
            skLineSegment(sketch, "E562", {"start": v(-347.94, 20.4) * mm, "end": v(-347.74, 31.5) * mm});
            skPoint(sketch, "E563.visualSharp", {"position": v(-377.48, 20.07) * mm});
            skArc(sketch, "E563.filletArc", {"start": v(-377.36, 24.38) * mm, "mid": v(-376.25, 21.06) * mm, "end": v(-373.25, 19.25) * mm});
            skPoint(sketch, "E564.visualSharp", {"position": v(-377.11, 32.9) * mm});
            skArc(sketch, "E564.filletArc", {"start": v(-372.95, 33.56) * mm, "mid": v(-375.97, 31.9) * mm, "end": v(-377.24, 28.69) * mm});
            skPoint(sketch, "E565.visualSharp", {"position": v(-347.64, 37.56) * mm});
            skArc(sketch, "E565.filletArc", {"start": v(-347.74, 31.5) * mm, "mid": v(-349.49, 35.43) * mm, "end": v(-353.62, 36.61) * mm});
            skPoint(sketch, "E566.visualSharp", {"position": v(-348.05, 14.34) * mm});
            skArc(sketch, "E566.filletArc", {"start": v(-354, 15.5) * mm, "mid": v(-349.83, 16.53) * mm, "end": v(-347.94, 20.4) * mm});
            skPoint(sketch, "E567.endSnap0", {"position": v(-347.84, 25.95) * mm});
            skLineSegment(sketch, "E568", {"start": v(-349.93, 94.63) * mm, "end": v(-346.9, 97.7) * mm});
            skLineSegment(sketch, "E569", {"start": v(-340.46, 98.36) * mm, "end": v(-324.2, 87.46) * mm});
            skLineSegment(sketch, "E570", {"start": v(-350.4, 88.07) * mm, "end": v(-338.83, 72.23) * mm});
            skLineSegment(sketch, "E571", {"start": v(-331.06, 71.7) * mm, "end": v(-323.37, 79.72) * mm});
            skPoint(sketch, "E572.visualSharp", {"position": v(-352.95, 91.55) * mm});
            skArc(sketch, "E572.filletArc", {"start": v(-349.93, 94.63) * mm, "mid": v(-351.37, 91.44) * mm, "end": v(-350.4, 88.07) * mm});
            skPoint(sketch, "E573.visualSharp", {"position": v(-343.96, 100.7) * mm});
            skArc(sketch, "E573.filletArc", {"start": v(-340.46, 98.36) * mm, "mid": v(-343.8, 99.2) * mm, "end": v(-346.9, 97.7) * mm});
            skPoint(sketch, "E574.visualSharp", {"position": v(-319.17, 84.08) * mm});
            skArc(sketch, "E574.filletArc", {"start": v(-323.37, 79.72) * mm, "mid": v(-321.98, 83.78) * mm, "end": v(-324.2, 87.46) * mm});
            skPoint(sketch, "E575.visualSharp", {"position": v(-335.26, 67.34) * mm});
            skArc(sketch, "E575.filletArc", {"start": v(-338.83, 72.23) * mm, "mid": v(-335.07, 70.15) * mm, "end": v(-331.06, 71.7) * mm});
            skPoint(sketch, "E576.endSnap0", {"position": v(-327.22, 75.71) * mm});
            skLineSegment(sketch, "E577", {"start": v(-319.14, 116.81) * mm, "end": v(-315.25, 118.67) * mm});
            skLineSegment(sketch, "E578", {"start": v(-308.96, 117.1) * mm, "end": v(-297.4, 101.3) * mm});
            skLineSegment(sketch, "E579", {"start": v(-321.82, 110.81) * mm, "end": v(-316.34, 91.97) * mm});
            skLineSegment(sketch, "E580", {"start": v(-309.21, 88.83) * mm, "end": v(-299.25, 93.74) * mm});
            skPoint(sketch, "E581.visualSharp", {"position": v(-323.02, 114.95) * mm});
            skArc(sketch, "E581.filletArc", {"start": v(-319.14, 116.81) * mm, "mid": v(-321.58, 114.3) * mm, "end": v(-321.82, 110.81) * mm});
            skPoint(sketch, "E582.visualSharp", {"position": v(-311.45, 120.5) * mm});
            skArc(sketch, "E582.filletArc", {"start": v(-308.96, 117.1) * mm, "mid": v(-311.82, 119.02) * mm, "end": v(-315.25, 118.67) * mm});
            skPoint(sketch, "E583.visualSharp", {"position": v(-293.82, 96.42) * mm});
            skArc(sketch, "E583.filletArc", {"start": v(-299.25, 93.74) * mm, "mid": v(-296.56, 97.1) * mm, "end": v(-297.4, 101.3) * mm});
            skPoint(sketch, "E584.visualSharp", {"position": v(-314.65, 86.16) * mm});
            skArc(sketch, "E584.filletArc", {"start": v(-316.34, 91.97) * mm, "mid": v(-313.5, 88.74) * mm, "end": v(-309.21, 88.83) * mm});
            skPoint(sketch, "E585.endSnap0", {"position": v(-304.23, 91.29) * mm});
            skLineSegment(sketch, "E586.MirrorCS", {"start": v(-234.15, 116.72) * mm, "end": v(-238.03, 118.59) * mm});
            skLineSegment(sketch, "E587.MirrorCS", {"start": v(-203.4, 94.47) * mm, "end": v(-206.42, 97.55) * mm});
            skLineSegment(sketch, "E588.MirrorCS", {"start": v(-183.14, 62.25) * mm, "end": v(-184.77, 66.23) * mm});
            skArc(sketch, "E589.MirrorCS", {"start": v(-201.9, 45.72) * mm, "mid": v(-206.16, 45.23) * mm, "end": v(-209.28, 48.18) * mm});
            skArc(sketch, "E590.MirrorCS", {"start": v(-213.37, 58.5) * mm, "mid": v(-213.12, 62.8) * mm, "end": v(-209.67, 65.36) * mm});
            skArc(sketch, "E591.MirrorCS", {"start": v(-214.55, 72.1) * mm, "mid": v(-218.32, 70.03) * mm, "end": v(-222.32, 71.59) * mm});
            skArc(sketch, "E592.MirrorCS", {"start": v(-183.14, 62.25) * mm, "mid": v(-183.02, 58.75) * mm, "end": v(-185.19, 56) * mm});
            skLineSegment(sketch, "E593.MirrorCS", {"start": v(-244.13, 88.76) * mm, "end": v(-254.09, 93.7) * mm});
            skArc(sketch, "E594.MirrorCS", {"start": v(-234.15, 116.72) * mm, "mid": v(-231.71, 114.2) * mm, "end": v(-231.48, 110.71) * mm});
            skArc(sketch, "E595.MirrorCS", {"start": v(-244.33, 117.02) * mm, "mid": v(-241.46, 118.94) * mm, "end": v(-238.03, 118.59) * mm});
            skArc(sketch, "E596.MirrorCS", {"start": v(-203.4, 94.47) * mm, "mid": v(-201.97, 91.27) * mm, "end": v(-202.94, 87.91) * mm});
            skArc(sketch, "E597.MirrorCS", {"start": v(-254.09, 93.7) * mm, "mid": v(-256.77, 97.05) * mm, "end": v(-255.93, 101.26) * mm});
            skArc(sketch, "E598.MirrorCS", {"start": v(-237, 91.88) * mm, "mid": v(-239.84, 88.66) * mm, "end": v(-244.13, 88.76) * mm});
            skLineSegment(sketch, "E599.MirrorCS", {"start": v(-209.28, 48.18) * mm, "end": v(-213.37, 58.5) * mm});
            skArc(sketch, "E600.MirrorCS", {"start": v(-190.5, 69.29) * mm, "mid": v(-187.08, 68.8) * mm, "end": v(-184.77, 66.23) * mm});
            skArc(sketch, "E601.MirrorCS", {"start": v(-212.87, 98.22) * mm, "mid": v(-209.52, 99.05) * mm, "end": v(-206.42, 97.55) * mm});
            skLineSegment(sketch, "E602.MirrorCS", {"start": v(-222.32, 71.59) * mm, "end": v(-230, 79.62) * mm});
            skArc(sketch, "E603.MirrorCS", {"start": v(-230, 79.62) * mm, "mid": v(-231.38, 83.68) * mm, "end": v(-229.15, 87.35) * mm});
            skPoint(sketch, "E604.MirrorP", {"position": v(-241.83, 120.42) * mm});
            skPoint(sketch, "E605.MirrorP", {"position": v(-226.16, 75.6) * mm});
            skPoint(sketch, "E606.MirrorP", {"position": v(-259.52, 96.38) * mm});
            skLineSegment(sketch, "E607.MirrorCS", {"start": v(-244.33, 117.02) * mm, "end": v(-255.93, 101.26) * mm});
            skPoint(sketch, "E608.MirrorP", {"position": v(-181.51, 58.26) * mm});
            skLineSegment(sketch, "E609.MirrorCS", {"start": v(-231.48, 110.71) * mm, "end": v(-237, 91.88) * mm});
            skPoint(sketch, "E610.MirrorP", {"position": v(-238.7, 86.08) * mm});
            skPoint(sketch, "E611.MirrorP", {"position": v(-200.4, 91.39) * mm});
            skPoint(sketch, "E612.MirrorP", {"position": v(-186.37, 70.14) * mm});
            skPoint(sketch, "E613.MirrorP", {"position": v(-249.11, 91.23) * mm});
            skLineSegment(sketch, "E614.MirrorCS", {"start": v(-202.94, 87.91) * mm, "end": v(-214.55, 72.1) * mm});
            skPoint(sketch, "E615.MirrorP", {"position": v(-209.37, 100.56) * mm});
            skPoint(sketch, "E616.MirrorP", {"position": v(-215.6, 64.14) * mm});
            skLineSegment(sketch, "E617.MirrorCS", {"start": v(-185.19, 56) * mm, "end": v(-201.9, 45.72) * mm});
            skPoint(sketch, "E618.MirrorP", {"position": v(-234.19, 84) * mm});
            skPoint(sketch, "E619.MirrorP", {"position": v(-207.06, 42.55) * mm});
            skLineSegment(sketch, "E620.MirrorCS", {"start": v(-190.5, 69.29) * mm, "end": v(-209.67, 65.36) * mm});
            skPoint(sketch, "E621.MirrorP", {"position": v(-230.27, 114.85) * mm});
            skPoint(sketch, "E622.MirrorP", {"position": v(-218.13, 67.21) * mm});
            skPoint(sketch, "E623.MirrorP", {"position": v(-211.33, 53.34) * mm});
            skLineSegment(sketch, "E624.MirrorCS", {"start": v(-212.87, 98.22) * mm, "end": v(-229.15, 87.35) * mm});
            skLineSegment(sketch, "E625.MirrorCS", {"start": v(-370.26, -10.64) * mm, "end": v(-368.62, -14.62) * mm});
            skLineSegment(sketch, "E626.MirrorCS", {"start": v(-349.93, -42.82) * mm, "end": v(-346.9, -45.9) * mm});
            skLineSegment(sketch, "E627.MirrorCS", {"start": v(-319.14, -65) * mm, "end": v(-315.25, -66.86) * mm});
            skArc(sketch, "E628.MirrorCS", {"start": v(-370.26, -10.64) * mm, "mid": v(-370.4, -7.14) * mm, "end": v(-368.23, -4.39) * mm});
            skArc(sketch, "E629.MirrorCS", {"start": v(-308.96, -65.28) * mm, "mid": v(-311.82, -67.2) * mm, "end": v(-315.25, -66.86) * mm});
            skArc(sketch, "E630.MirrorCS", {"start": v(-319.14, -65) * mm, "mid": v(-321.58, -62.5) * mm, "end": v(-321.82, -59) * mm});
            skLineSegment(sketch, "E631.MirrorCS", {"start": v(-309.21, -37.02) * mm, "end": v(-299.25, -41.93) * mm});
            skLineSegment(sketch, "E632.MirrorCS", {"start": v(-344.15, 3.49) * mm, "end": v(-340.04, -6.84) * mm});
            skLineSegment(sketch, "E633.MirrorCS", {"start": v(-331.06, -19.9) * mm, "end": v(-323.37, -27.9) * mm});
            skArc(sketch, "E634.MirrorCS", {"start": v(-349.93, -42.82) * mm, "mid": v(-351.37, -39.63) * mm, "end": v(-350.4, -36.26) * mm});
            skArc(sketch, "E635.MirrorCS", {"start": v(-340.46, -46.55) * mm, "mid": v(-343.8, -47.38) * mm, "end": v(-346.9, -45.9) * mm});
            skArc(sketch, "E636.MirrorCS", {"start": v(-362.9, -17.67) * mm, "mid": v(-366.3, -17.18) * mm, "end": v(-368.62, -14.62) * mm});
            skPoint(sketch, "E637.MirrorP", {"position": v(-335.26, -15.53) * mm});
            skPoint(sketch, "E638.MirrorP", {"position": v(-342.1, -1.68) * mm});
            skLineSegment(sketch, "E639.MirrorCS", {"start": v(-308.96, -65.28) * mm, "end": v(-297.4, -49.5) * mm});
            skArc(sketch, "E640.MirrorCS", {"start": v(-340.04, -6.84) * mm, "mid": v(-340.29, -11.12) * mm, "end": v(-343.73, -13.7) * mm});
            skLineSegment(sketch, "E641.MirrorCS", {"start": v(-362.9, -17.67) * mm, "end": v(-343.73, -13.7) * mm});
            skLineSegment(sketch, "E642.MirrorCS", {"start": v(-340.46, -46.55) * mm, "end": v(-324.2, -35.65) * mm});
            skPoint(sketch, "E643.MirrorP", {"position": v(-346.4, 9.1) * mm});
            skPoint(sketch, "E644.MirrorP", {"position": v(-319.17, -32.27) * mm});
            skArc(sketch, "E645.MirrorCS", {"start": v(-316.34, -40.16) * mm, "mid": v(-313.5, -36.93) * mm, "end": v(-309.21, -37.02) * mm});
            skArc(sketch, "E646.MirrorCS", {"start": v(-299.25, -41.93) * mm, "mid": v(-296.56, -45.28) * mm, "end": v(-297.4, -49.5) * mm});
            skArc(sketch, "E647.MirrorCS", {"start": v(-323.37, -27.9) * mm, "mid": v(-321.98, -31.97) * mm, "end": v(-324.2, -35.65) * mm});
            skPoint(sketch, "E648.MirrorP", {"position": v(-337.8, -12.46) * mm});
            skPoint(sketch, "E649.MirrorP", {"position": v(-343.96, -48.9) * mm});
            skPoint(sketch, "E650.MirrorP", {"position": v(-304.23, -39.48) * mm});
            skPoint(sketch, "E651.MirrorP", {"position": v(-352.95, -39.74) * mm});
            skPoint(sketch, "E652.MirrorP", {"position": v(-367.02, -18.52) * mm});
            skArc(sketch, "E653.MirrorCS", {"start": v(-338.83, -20.42) * mm, "mid": v(-335.07, -18.35) * mm, "end": v(-331.06, -19.9) * mm});
            skPoint(sketch, "E654.MirrorP", {"position": v(-314.65, -34.35) * mm});
            skArc(sketch, "E655.MirrorCS", {"start": v(-351.54, 5.93) * mm, "mid": v(-347.28, 6.43) * mm, "end": v(-344.15, 3.49) * mm});
            skLineSegment(sketch, "E656.MirrorCS", {"start": v(-321.82, -59) * mm, "end": v(-316.34, -40.16) * mm});
            skPoint(sketch, "E657.MirrorP", {"position": v(-371.9, -6.66) * mm});
            skLineSegment(sketch, "E658.MirrorCS", {"start": v(-350.4, -36.26) * mm, "end": v(-338.83, -20.42) * mm});
            skLineSegment(sketch, "E659.MirrorCS", {"start": v(-368.23, -4.39) * mm, "end": v(-351.54, 5.93) * mm});
            skPoint(sketch, "E660.MirrorP", {"position": v(-293.82, -44.6) * mm});
            skPoint(sketch, "E661.MirrorP", {"position": v(-311.45, -68.68) * mm});
            skPoint(sketch, "E662.MirrorP", {"position": v(-327.22, -23.9) * mm});
            skPoint(sketch, "E663.MirrorP", {"position": v(-323.02, -63.14) * mm});
            skLineSegment(sketch, "E664.MirrorCS", {"start": v(-234.15, -64.91) * mm, "end": v(-238.03, -66.78) * mm});
            skLineSegment(sketch, "E665.MirrorCS", {"start": v(-203.4, -42.66) * mm, "end": v(-206.42, -45.74) * mm});
            skLineSegment(sketch, "E666.MirrorCS", {"start": v(-183.14, -10.44) * mm, "end": v(-184.77, -14.43) * mm});
            skArc(sketch, "E667.MirrorCS", {"start": v(-183.14, -10.44) * mm, "mid": v(-183.02, -6.94) * mm, "end": v(-185.19, -4.2) * mm});
            skArc(sketch, "E668.MirrorCS", {"start": v(-213.37, -6.7) * mm, "mid": v(-213.12, -10.99) * mm, "end": v(-209.67, -13.55) * mm});
            skLineSegment(sketch, "E669.MirrorCS", {"start": v(-244.13, -36.95) * mm, "end": v(-254.09, -41.88) * mm});
            skArc(sketch, "E670.MirrorCS", {"start": v(-234.15, -64.91) * mm, "mid": v(-231.71, -62.4) * mm, "end": v(-231.48, -58.9) * mm});
            skArc(sketch, "E671.MirrorCS", {"start": v(-244.33, -65.21) * mm, "mid": v(-241.46, -67.13) * mm, "end": v(-238.03, -66.78) * mm});
            skArc(sketch, "E672.MirrorCS", {"start": v(-203.4, -42.66) * mm, "mid": v(-201.97, -39.47) * mm, "end": v(-202.94, -36.1) * mm});
            skLineSegment(sketch, "E673.MirrorCS", {"start": v(-222.32, -19.78) * mm, "end": v(-230, -27.8) * mm});
            skArc(sketch, "E674.MirrorCS", {"start": v(-254.09, -41.88) * mm, "mid": v(-256.77, -45.24) * mm, "end": v(-255.93, -49.45) * mm});
            skArc(sketch, "E675.MirrorCS", {"start": v(-237, -40.08) * mm, "mid": v(-239.84, -36.85) * mm, "end": v(-244.13, -36.95) * mm});
            skLineSegment(sketch, "E676.MirrorCS", {"start": v(-209.28, 3.63) * mm, "end": v(-213.37, -6.7) * mm});
            skArc(sketch, "E677.MirrorCS", {"start": v(-190.5, -17.48) * mm, "mid": v(-187.08, -16.99) * mm, "end": v(-184.77, -14.43) * mm});
            skArc(sketch, "E678.MirrorCS", {"start": v(-201.9, 6.09) * mm, "mid": v(-206.16, 6.58) * mm, "end": v(-209.28, 3.63) * mm});
            skArc(sketch, "E679.MirrorCS", {"start": v(-214.55, -20.28) * mm, "mid": v(-218.32, -18.22) * mm, "end": v(-222.32, -19.78) * mm});
            skArc(sketch, "E680.MirrorCS", {"start": v(-230, -27.8) * mm, "mid": v(-231.38, -31.87) * mm, "end": v(-229.15, -35.54) * mm});
            skArc(sketch, "E681.MirrorCS", {"start": v(-212.87, -46.41) * mm, "mid": v(-209.52, -47.24) * mm, "end": v(-206.42, -45.74) * mm});
            skLineSegment(sketch, "E682.MirrorCS", {"start": v(-190.5, -17.48) * mm, "end": v(-209.67, -13.55) * mm});
            skLineSegment(sketch, "E683.MirrorCS", {"start": v(-202.94, -36.1) * mm, "end": v(-214.55, -20.28) * mm});
            skPoint(sketch, "E684.MirrorP", {"position": v(-230.27, -63.04) * mm});
            skLineSegment(sketch, "E685.MirrorCS", {"start": v(-212.87, -46.41) * mm, "end": v(-229.15, -35.54) * mm});
            skPoint(sketch, "E686.MirrorP", {"position": v(-249.11, -39.42) * mm});
            skPoint(sketch, "E687.MirrorP", {"position": v(-218.13, -15.4) * mm});
            skPoint(sketch, "E688.MirrorP", {"position": v(-241.83, -68.6) * mm});
            skPoint(sketch, "E689.MirrorP", {"position": v(-226.16, -23.8) * mm});
            skPoint(sketch, "E690.MirrorP", {"position": v(-259.52, -44.57) * mm});
            skPoint(sketch, "E691.MirrorP", {"position": v(-181.51, -6.45) * mm});
            skPoint(sketch, "E692.MirrorP", {"position": v(-207.06, 9.26) * mm});
            skLineSegment(sketch, "E693.MirrorCS", {"start": v(-231.48, -58.9) * mm, "end": v(-237, -40.08) * mm});
            skPoint(sketch, "E694.MirrorP", {"position": v(-238.7, -34.27) * mm});
            skPoint(sketch, "E695.MirrorP", {"position": v(-215.6, -12.33) * mm});
            skPoint(sketch, "E696.MirrorP", {"position": v(-200.4, -39.58) * mm});
            skLineSegment(sketch, "E697.MirrorCS", {"start": v(-244.33, -65.21) * mm, "end": v(-255.93, -49.45) * mm});
            skLineSegment(sketch, "E698.MirrorCS", {"start": v(-185.19, -4.2) * mm, "end": v(-201.9, 6.09) * mm});
            skPoint(sketch, "E699.MirrorP", {"position": v(-234.19, -32.18) * mm});
            skPoint(sketch, "E700.MirrorP", {"position": v(-186.37, -18.33) * mm});
            skPoint(sketch, "E701.MirrorP", {"position": v(-209.37, -48.75) * mm});
            skPoint(sketch, "E702.MirrorP", {"position": v(-211.33, -1.53) * mm});
            skSolve(sketch);
        }
        {
            var Q0;
            Q0=makeQuery(id+"F0.imprint","IMPRINT",FACE,{"disambiguationData":[TD([[makeQuery(id+"F0.imprint","IMPRINT",EDGE,{"derivedFrom":sQuery(id+"F0.wireOp",EDGE,"E16")}),-1.0]])]});
            var Q1;
            Q1=makeQuery(id+"F0.imprint","IMPRINT",FACE,{"disambiguationData":[TD([[makeQuery(id+"F0.imprint","IMPRINT",EDGE,{"derivedFrom":sQuery(id+"F0.wireOp",EDGE,"E43")}),-1.0]])]});
            var Q2;
            Q2=makeQuery(id+"F0.imprint","IMPRINT",FACE,{"disambiguationData":[TD([[makeQuery(id+"F0.imprint","IMPRINT",EDGE,{"derivedFrom":sQuery(id+"F0.wireOp",EDGE,"E329")}),-1.0]])]});
            var Q3;
            Q3=makeQuery(id+"F0.imprint","IMPRINT",FACE,{"disambiguationData":[TD([[makeQuery(id+"F0.imprint","IMPRINT",EDGE,{"derivedFrom":sQuery(id+"F0.wireOp",EDGE,"E25")}),-1.0]])]});
            var Q4;
            Q4=makeQuery(id+"F0.imprint","IMPRINT",FACE,{"disambiguationData":[TD([[makeQuery(id+"F0.imprint","IMPRINT",EDGE,{"derivedFrom":sQuery(id+"F0.wireOp",EDGE,"E64.MirrorCS")}),-1.0]])]});
            var Q5;
            Q5=makeQuery(id+"F0.imprint","IMPRINT",FACE,{"disambiguationData":[TD([[makeQuery(id+"F0.imprint","IMPRINT",EDGE,{"derivedFrom":sQuery(id+"F0.wireOp",EDGE,"E52")}),-1.0]])]});
            var Q6;
            Q6=makeQuery(id+"F0.imprint","IMPRINT",FACE,{"disambiguationData":[TD([[makeQuery(id+"F0.imprint","IMPRINT",EDGE,{"derivedFrom":sQuery(id+"F0.wireOp",EDGE,"E34")}),-1.0]])]});
            var Q7;
            Q7=makeQuery(id+"F0.imprint","IMPRINT",FACE,{"disambiguationData":[TD([[makeQuery(id+"F0.imprint","IMPRINT",EDGE,{"derivedFrom":sQuery(id+"F0.wireOp",EDGE,"E7")}),-1.0]])]});
            var Q8;
            Q8=makeQuery(id+"F0.imprint","IMPRINT",FACE,{"disambiguationData":[TD([[makeQuery(id+"F0.imprint","IMPRINT",EDGE,{"derivedFrom":sQuery(id+"F0.wireOp",EDGE,"E61.MirrorCS")}),-1.0]])]});
            var Q9;
            Q9=makeQuery(id+"F0.imprint","IMPRINT",FACE,{"disambiguationData":[TD([[makeQuery(id+"F0.imprint","IMPRINT",EDGE,{"derivedFrom":sQuery(id+"F0.wireOp",EDGE,"E141.MirrorCS")}),1.0]])]});
            var Q10;
            Q10=makeQuery(id+"F0.imprint","IMPRINT",FACE,{"disambiguationData":[TD([[makeQuery(id+"F0.imprint","IMPRINT",EDGE,{"derivedFrom":sQuery(id+"F0.wireOp",EDGE,"E140.MirrorCS")}),1.0]])]});
            var Q11;
            Q11=makeQuery(id+"F0.imprint","IMPRINT",FACE,{"disambiguationData":[TD([[makeQuery(id+"F0.imprint","IMPRINT",EDGE,{"derivedFrom":sQuery(id+"F0.wireOp",EDGE,"E177.MirrorCS")}),1.0]])]});
            var Q12;
            Q12=makeQuery(id+"F0.imprint","IMPRINT",FACE,{"disambiguationData":[TD([[makeQuery(id+"F0.imprint","IMPRINT",EDGE,{"derivedFrom":sQuery(id+"F0.wireOp",EDGE,"E286.MirrorCS")}),-1.0]])]});
            var Q13;
            Q13=makeQuery(id+"F0.imprint","IMPRINT",FACE,{"disambiguationData":[TD([[makeQuery(id+"F0.imprint","IMPRINT",EDGE,{"derivedFrom":sQuery(id+"F0.wireOp",EDGE,"E277")}),-1.0]])]});
            var Q14;
            Q14=makeQuery(id+"F0.imprint","IMPRINT",FACE,{"disambiguationData":[TD([[makeQuery(id+"F0.imprint","IMPRINT",EDGE,{"derivedFrom":sQuery(id+"F0.wireOp",EDGE,"E167.MirrorCS")}),-1.0]])]});
            var Q15;
            Q15=makeQuery(id+"F0.imprint","IMPRINT",FACE,{"disambiguationData":[TD([[makeQuery(id+"F0.imprint","IMPRINT",EDGE,{"derivedFrom":sQuery(id+"F0.wireOp",EDGE,"E268")}),-1.0]])]});
            var Q16;
            {var subQ10=sQuery(id+"F0.wireOp",EDGE,"E174.MirrorCS");Q16=makeQuery(id+"F0.imprint","IMPRINT",FACE,{"disambiguationData":[TD([[makeQuery(id+"F0.imprint","IMPRINT",EDGE,{"derivedFrom":subQ10}),-1.0]])]});}
            var Q17;
            {var subQ9=sQuery(id+"F0.wireOp",EDGE,"E144.MirrorCS");Q17=makeQuery(id+"F0.imprint","IMPRINT",FACE,{"disambiguationData":[TD([[makeQuery(id+"F0.imprint","IMPRINT",EDGE,{"derivedFrom":subQ9}),1.0]])]});}
            var Q18;
            {var subQ73=sQuery(id+"F0.wireOp",EDGE,"E10");Q18=makeQuery(id+"F0.imprint","IMPRINT",FACE,{"disambiguationData":[TD([[makeQuery(id+"F0.imprint","IMPRINT",EDGE,{"derivedFrom":subQ73}),-1.0]])]});}
            var Q19;
            Q19=makeQuery(id+"F0.imprint","IMPRINT",FACE,{"disambiguationData":[TD([[makeQuery(id+"F0.imprint","IMPRINT",EDGE,{"derivedFrom":sQuery(id+"F0.wireOp",EDGE,"E147.MirrorCS")}),-1.0]])]});
            var Q20;
            {var subQ0=sQuery(id+"F0.wireOp",EDGE,"E5");var subQ1=sQuery(id+"F0.wireOp",EDGE,"E0");var subQ2=makeQuery(id+"F0.imprint","INTERSECT",VERTEX,{"derivedFrom":[subQ1,subQ0]});Q20=makeQuery(id+"F0.imprint","IMPRINT",FACE,{"disambiguationData":[TD([[makeQuery(id+"F0.imprint","IMPRINT",EDGE,{"disambiguationData":[TD([[subQ2,1.0]])],"derivedFrom":subQ1}),1.0]])]});}
            var Q21;
            {var subQ4=sQuery(id+"F0.wireOp",EDGE,"E165.MirrorCS");Q21=makeQuery(id+"F0.imprint","IMPRINT",FACE,{"disambiguationData":[TD([[makeQuery(id+"F0.imprint","IMPRINT",EDGE,{"derivedFrom":subQ4}),-1.0]])]});}
            var Q22;
            {var subQ0=sQuery(id+"F0.wireOp",EDGE,"E6");var subQ1=sQuery(id+"F0.wireOp",EDGE,"E0");var subQ2=makeQuery(id+"F0.imprint","INTERSECT",VERTEX,{"derivedFrom":[subQ1,subQ0]});Q22=makeQuery(id+"F0.imprint","IMPRINT",FACE,{"disambiguationData":[TD([[makeQuery(id+"F0.imprint","IMPRINT",EDGE,{"disambiguationData":[TD([[subQ2,1.0]])],"derivedFrom":subQ1}),1.0]])]});}
            var Q23;
            Q23=makeQuery(id+"F0.imprint","IMPRINT",FACE,{"disambiguationData":[TD([[makeQuery(id+"F0.imprint","IMPRINT",EDGE,{"derivedFrom":sQuery(id+"F0.wireOp",EDGE,"E298")}),-1.0]])]});
            var Q24;
            Q24=makeQuery(id+"F0.imprint","IMPRINT",FACE,{"disambiguationData":[TD([[makeQuery(id+"F0.imprint","IMPRINT",EDGE,{"derivedFrom":sQuery(id+"F0.wireOp",EDGE,"E62.MirrorCS")}),-1.0]])]});
            var Q25;
            {var subQ0=sQuery(id+"F0.wireOp",EDGE,"E6");var subQ1=sQuery(id+"F0.wireOp",EDGE,"E0");var subQ2=makeQuery(id+"F0.imprint","INTERSECT",VERTEX,{"derivedFrom":[subQ1,subQ0]});Q25=makeQuery(id+"F0.imprint","IMPRINT",FACE,{"disambiguationData":[TD([[makeQuery(id+"F0.imprint","IMPRINT",EDGE,{"disambiguationData":[TD([[subQ2,-1.0]])],"derivedFrom":subQ1}),1.0]])]});}
            var Q26;
            {var subQ5=sQuery(id+"F0.wireOp",EDGE,"E37");Q26=makeQuery(id+"F0.imprint","IMPRINT",FACE,{"disambiguationData":[TD([[makeQuery(id+"F0.imprint","IMPRINT",EDGE,{"derivedFrom":subQ5}),1.0]])]});}
            var Q27;
            {var subQ5=sQuery(id+"F0.wireOp",EDGE,"E55");Q27=makeQuery(id+"F0.imprint","IMPRINT",FACE,{"disambiguationData":[TD([[makeQuery(id+"F0.imprint","IMPRINT",EDGE,{"derivedFrom":subQ5}),1.0]])]});}
            var Q28;
            {var subQ5=sQuery(id+"F0.wireOp",EDGE,"E163.MirrorCS");Q28=makeQuery(id+"F0.imprint","IMPRINT",FACE,{"disambiguationData":[TD([[makeQuery(id+"F0.imprint","IMPRINT",EDGE,{"derivedFrom":subQ5}),-1.0]])]});}
            var Q29;
            {var subQ5=sQuery(id+"F0.wireOp",EDGE,"E89.MirrorCS");Q29=makeQuery(id+"F0.imprint","IMPRINT",FACE,{"disambiguationData":[TD([[makeQuery(id+"F0.imprint","IMPRINT",EDGE,{"derivedFrom":subQ5}),-1.0]])]});}
            var Q30;
            {var subQ5=sQuery(id+"F0.wireOp",EDGE,"E144.MirrorCS");Q30=makeQuery(id+"F0.imprint","IMPRINT",FACE,{"disambiguationData":[TD([[makeQuery(id+"F0.imprint","IMPRINT",EDGE,{"derivedFrom":subQ5}),-1.0]])]});}
            var Q31;
            Q31=makeQuery(id+"F0.imprint","IMPRINT",FACE,{"disambiguationData":[TD([[makeQuery(id+"F0.imprint","IMPRINT",EDGE,{"derivedFrom":sQuery(id+"F0.wireOp",EDGE,"E66.MirrorCS")}),-1.0]])]});
            var Q32;
            {var subQ0=sQuery(id+"F0.wireOp",EDGE,"E187.MirrorCS");Q32=makeQuery(id+"F0.imprint","IMPRINT",FACE,{"disambiguationData":[TD([[makeQuery(id+"F0.imprint","IMPRINT",EDGE,{"derivedFrom":subQ0}),-1.0]])]});}
            var Q33;
            {var subQ5=sQuery(id+"F0.wireOp",EDGE,"E90.MirrorCS");Q33=makeQuery(id+"F0.imprint","IMPRINT",FACE,{"disambiguationData":[TD([[makeQuery(id+"F0.imprint","IMPRINT",EDGE,{"derivedFrom":subQ5}),-1.0]])]});}
            var Q34;
            {var subQ5=sQuery(id+"F0.wireOp",EDGE,"E95.MirrorCS");Q34=makeQuery(id+"F0.imprint","IMPRINT",FACE,{"disambiguationData":[TD([[makeQuery(id+"F0.imprint","IMPRINT",EDGE,{"derivedFrom":subQ5}),-1.0]])]});}
            var Q35;
            {var subQ5=sQuery(id+"F0.wireOp",EDGE,"E145.MirrorCS");Q35=makeQuery(id+"F0.imprint","IMPRINT",FACE,{"disambiguationData":[TD([[makeQuery(id+"F0.imprint","IMPRINT",EDGE,{"derivedFrom":subQ5}),-1.0]])]});}
            var Q36;
            Q36=makeQuery(id+"F0.imprint","IMPRINT",FACE,{"disambiguationData":[TD([[makeQuery(id+"F0.imprint","IMPRINT",EDGE,{"derivedFrom":sQuery(id+"F0.wireOp",EDGE,"E65.MirrorCS")}),-1.0]])]});
            var Q37;
            {var subQ5=sQuery(id+"F0.wireOp",EDGE,"E91.MirrorCS");Q37=makeQuery(id+"F0.imprint","IMPRINT",FACE,{"disambiguationData":[TD([[makeQuery(id+"F0.imprint","IMPRINT",EDGE,{"derivedFrom":subQ5}),-1.0]])]});}
            var Q38;
            Q38=makeQuery(id+"F0.imprint","IMPRINT",FACE,{"disambiguationData":[TD([[makeQuery(id+"F0.imprint","IMPRINT",EDGE,{"derivedFrom":sQuery(id+"F0.wireOp",EDGE,"E63.MirrorCS")}),-1.0]])]});
            var Q39;
            Q39=makeQuery(id+"F0.imprint","IMPRINT",FACE,{"disambiguationData":[TD([[makeQuery(id+"F0.imprint","IMPRINT",EDGE,{"derivedFrom":sQuery(id+"F0.wireOp",EDGE,"E146.MirrorCS")}),-1.0]])]});
            var Q40;
            {var subQ5=sQuery(id+"F0.wireOp",EDGE,"E88.MirrorCS");Q40=makeQuery(id+"F0.imprint","IMPRINT",FACE,{"disambiguationData":[TD([[makeQuery(id+"F0.imprint","IMPRINT",EDGE,{"derivedFrom":subQ5}),-1.0]])]});}
            var Q41;
            {var subQ0=sQuery(id+"F0.wireOp",EDGE,"E5");var subQ1=sQuery(id+"F0.wireOp",EDGE,"E1");var subQ2=makeQuery(id+"F0.imprint","INTERSECT",VERTEX,{"derivedFrom":[subQ1,subQ0]});Q41=makeQuery(id+"F0.imprint","IMPRINT",FACE,{"disambiguationData":[TD([[makeQuery(id+"F0.imprint","IMPRINT",EDGE,{"disambiguationData":[TD([[subQ2,-1.0]])],"derivedFrom":subQ1}),1.0]])]});}
            var Q42;
            {var subQ5=sQuery(id+"F0.wireOp",EDGE,"E220.MirrorCS");Q42=makeQuery(id+"F0.imprint","IMPRINT",FACE,{"disambiguationData":[TD([[makeQuery(id+"F0.imprint","IMPRINT",EDGE,{"derivedFrom":subQ5}),1.0]])]});}
            var Q43;
            {var subQ0=sQuery(id+"F0.wireOp",EDGE,"E5");var subQ1=sQuery(id+"F0.wireOp",EDGE,"E1");var subQ2=makeQuery(id+"F0.imprint","INTERSECT",VERTEX,{"derivedFrom":[subQ1,subQ0]});Q43=makeQuery(id+"F0.imprint","IMPRINT",FACE,{"disambiguationData":[TD([[makeQuery(id+"F0.imprint","IMPRINT",EDGE,{"disambiguationData":[TD([[subQ2,1.0]])],"derivedFrom":subQ1}),1.0]])]});}
            var Q44;
            {var subQ5=sQuery(id+"F0.wireOp",EDGE,"E291.MirrorCS");Q44=makeQuery(id+"F0.imprint","IMPRINT",FACE,{"disambiguationData":[TD([[makeQuery(id+"F0.imprint","IMPRINT",EDGE,{"derivedFrom":subQ5}),1.0]])]});}
            var Q45;
            {var subQ0=sQuery(id+"F0.wireOp",EDGE,"E4");var subQ1=sQuery(id+"F0.wireOp",EDGE,"E1");var subQ2=makeQuery(id+"F0.imprint","INTERSECT",VERTEX,{"derivedFrom":[subQ1,subQ0]});Q45=makeQuery(id+"F0.imprint","IMPRINT",FACE,{"disambiguationData":[TD([[makeQuery(id+"F0.imprint","IMPRINT",EDGE,{"disambiguationData":[TD([[subQ2,-1.0]])],"derivedFrom":subQ1}),1.0]])]});}
            var Q46;
            {var subQ5=sQuery(id+"F0.wireOp",EDGE,"E19");Q46=makeQuery(id+"F0.imprint","IMPRINT",FACE,{"disambiguationData":[TD([[makeQuery(id+"F0.imprint","IMPRINT",EDGE,{"derivedFrom":subQ5}),1.0]])]});}
            var Q47;
            {var subQ5=sQuery(id+"F0.wireOp",EDGE,"E216.MirrorCS");Q47=makeQuery(id+"F0.imprint","IMPRINT",FACE,{"disambiguationData":[TD([[makeQuery(id+"F0.imprint","IMPRINT",EDGE,{"derivedFrom":subQ5}),1.0]])]});}
            var Q48;
            {var subQ5=sQuery(id+"F0.wireOp",EDGE,"E46");Q48=makeQuery(id+"F0.imprint","IMPRINT",FACE,{"disambiguationData":[TD([[makeQuery(id+"F0.imprint","IMPRINT",EDGE,{"derivedFrom":subQ5}),1.0]])]});}
            var Q49;
            {var subQ5=sQuery(id+"F0.wireOp",EDGE,"E203.MirrorCS");Q49=makeQuery(id+"F0.imprint","IMPRINT",FACE,{"disambiguationData":[TD([[makeQuery(id+"F0.imprint","IMPRINT",EDGE,{"derivedFrom":subQ5}),1.0]])]});}
            var Q50;
            Q50=makeQuery(id+"F0.imprint","IMPRINT",FACE,{"disambiguationData":[TD([[makeQuery(id+"F0.imprint","IMPRINT",EDGE,{"derivedFrom":sQuery(id+"F0.wireOp",EDGE,"E152.MirrorCS")}),1.0]])]});
            var Q51;
            Q51=makeQuery(id+"F0.imprint","IMPRINT",FACE,{"disambiguationData":[TD([[makeQuery(id+"F0.imprint","IMPRINT",EDGE,{"derivedFrom":sQuery(id+"F0.wireOp",EDGE,"E173.MirrorCS")}),-1.0]])]});
            var Q52;
            {var subQ5=sQuery(id+"F0.wireOp",EDGE,"E200.MirrorCS");Q52=makeQuery(id+"F0.imprint","IMPRINT",FACE,{"disambiguationData":[TD([[makeQuery(id+"F0.imprint","IMPRINT",EDGE,{"derivedFrom":subQ5}),-1.0]])]});}
            var Q53;
            {var subQ5=sQuery(id+"F0.wireOp",EDGE,"E96.MirrorCS");Q53=makeQuery(id+"F0.imprint","IMPRINT",FACE,{"disambiguationData":[TD([[makeQuery(id+"F0.imprint","IMPRINT",EDGE,{"derivedFrom":subQ5}),-1.0]])]});}
            var Q54;
            {var subQ5=sQuery(id+"F0.wireOp",EDGE,"E10");Q54=makeQuery(id+"F0.imprint","IMPRINT",FACE,{"disambiguationData":[TD([[makeQuery(id+"F0.imprint","IMPRINT",EDGE,{"derivedFrom":subQ5}),1.0]])]});}
            var Q55;
            {var subQ5=sQuery(id+"F0.wireOp",EDGE,"E28");Q55=makeQuery(id+"F0.imprint","IMPRINT",FACE,{"disambiguationData":[TD([[makeQuery(id+"F0.imprint","IMPRINT",EDGE,{"derivedFrom":subQ5}),1.0]])]});}
            var Q56;
            {var subQ5=sQuery(id+"F0.wireOp",EDGE,"E280");Q56=makeQuery(id+"F0.imprint","IMPRINT",FACE,{"disambiguationData":[TD([[makeQuery(id+"F0.imprint","IMPRINT",EDGE,{"derivedFrom":subQ5}),1.0]])]});}
            var Q57;
            {var subQ5=sQuery(id+"F0.wireOp",EDGE,"E332");Q57=makeQuery(id+"F0.imprint","IMPRINT",FACE,{"disambiguationData":[TD([[makeQuery(id+"F0.imprint","IMPRINT",EDGE,{"derivedFrom":subQ5}),1.0]])]});}
            var Q58;
            {var subQ5=sQuery(id+"F0.wireOp",EDGE,"E189.MirrorCS");Q58=makeQuery(id+"F0.imprint","IMPRINT",FACE,{"disambiguationData":[TD([[makeQuery(id+"F0.imprint","IMPRINT",EDGE,{"derivedFrom":subQ5}),-1.0]])]});}
            var Q59;
            {var subQ0=sQuery(id+"F0.wireOp",EDGE,"E4");var subQ1=sQuery(id+"F0.wireOp",EDGE,"E1");var subQ2=makeQuery(id+"F0.imprint","INTERSECT",VERTEX,{"derivedFrom":[subQ1,subQ0]});Q59=makeQuery(id+"F0.imprint","IMPRINT",FACE,{"disambiguationData":[TD([[makeQuery(id+"F0.imprint","IMPRINT",EDGE,{"disambiguationData":[TD([[subQ2,1.0]])],"derivedFrom":subQ1}),1.0]])]});}
            var Q60;
            {var subQ0=sQuery(id+"F0.wireOp",EDGE,"E6");var subQ1=sQuery(id+"F0.wireOp",EDGE,"E1");var subQ2=makeQuery(id+"F0.imprint","INTERSECT",VERTEX,{"derivedFrom":[subQ1,subQ0]});Q60=makeQuery(id+"F0.imprint","IMPRINT",FACE,{"disambiguationData":[TD([[makeQuery(id+"F0.imprint","IMPRINT",EDGE,{"disambiguationData":[TD([[subQ2,-1.0]])],"derivedFrom":subQ1}),1.0]])]});}
            var Q61;
            {var subQ5=sQuery(id+"F0.wireOp",EDGE,"E212.MirrorCS");Q61=makeQuery(id+"F0.imprint","IMPRINT",FACE,{"disambiguationData":[TD([[makeQuery(id+"F0.imprint","IMPRINT",EDGE,{"derivedFrom":subQ5}),1.0]])]});}
            var Q62;
            Q62=makeQuery(id+"F0.imprint","IMPRINT",FACE,{"disambiguationData":[TD([[makeQuery(id+"F0.imprint","IMPRINT",EDGE,{"derivedFrom":sQuery(id+"F0.wireOp",EDGE,"E307.MirrorCS")}),-1.0]])]});
            var Q63;
            {var subQ5=sQuery(id+"F0.wireOp",EDGE,"E174.MirrorCS");Q63=makeQuery(id+"F0.imprint","IMPRINT",FACE,{"disambiguationData":[TD([[makeQuery(id+"F0.imprint","IMPRINT",EDGE,{"derivedFrom":subQ5}),1.0]])]});}
            var Q64;
            {var subQ0=sQuery(id+"F0.wireOp",EDGE,"E6");var subQ1=sQuery(id+"F0.wireOp",EDGE,"E1");var subQ2=makeQuery(id+"F0.imprint","INTERSECT",VERTEX,{"derivedFrom":[subQ1,subQ0]});Q64=makeQuery(id+"F0.imprint","IMPRINT",FACE,{"disambiguationData":[TD([[makeQuery(id+"F0.imprint","IMPRINT",EDGE,{"disambiguationData":[TD([[subQ2,1.0]])],"derivedFrom":subQ1}),1.0]])]});}
            extrude(context, id + "F1", {"entities" : qUnion([Q0, Q1, Q2, Q3, Q4, Q5, Q6, Q7, Q8, Q9, Q10, Q11, Q12, Q13, Q14, Q15, Q16, Q17, Q18, Q19, Q20, Q21, Q22, Q23, Q24, Q25, Q26, Q27, Q28, Q29, Q30, Q31, Q32, Q33, Q34, Q35, Q36, Q37, Q38, Q39, Q40, Q41, Q42, Q43, Q44, Q45, Q46, Q47, Q48, Q49, Q50, Q51, Q52, Q53, Q54, Q55, Q56, Q57, Q58, Q59, Q60, Q61, Q62, Q63, Q64]), "depth" : 12.7 * mm});
        }
        {
            var Q0;
            Q0=makeQuery(id+"F0.imprint","IMPRINT",FACE,{"disambiguationData":[TD([[makeQuery(id+"F0.imprint","IMPRINT",EDGE,{"derivedFrom":sQuery(id+"F0.wireOp",EDGE,"E353")}),-1.0]])]});
            var Q1;
            Q1=makeQuery(id+"F0.imprint","IMPRINT",FACE,{"disambiguationData":[TD([[makeQuery(id+"F0.imprint","IMPRINT",EDGE,{"derivedFrom":sQuery(id+"F0.wireOp",EDGE,"E400.MirrorCS")}),1.0]])]});
            var Q2;
            Q2=makeQuery(id+"F0.imprint","IMPRINT",FACE,{"disambiguationData":[TD([[makeQuery(id+"F0.imprint","IMPRINT",EDGE,{"derivedFrom":sQuery(id+"F0.wireOp",EDGE,"E320")}),-1.0]])]});
            var Q3;
            Q3=makeQuery(id+"F0.imprint","IMPRINT",FACE,{"disambiguationData":[TD([[makeQuery(id+"F0.imprint","IMPRINT",EDGE,{"derivedFrom":sQuery(id+"F0.wireOp",EDGE,"E477.MirrorCS")}),-1.0]])]});
            var Q4;
            {var subQ6=sQuery(id+"F0.wireOp",EDGE,"E443.MirrorCS");Q4=makeQuery(id+"F0.imprint","IMPRINT",FACE,{"disambiguationData":[TD([[makeQuery(id+"F0.imprint","IMPRINT",EDGE,{"derivedFrom":subQ6}),1.0]])]});}
            var Q5;
            Q5=makeQuery(id+"F0.imprint","IMPRINT",FACE,{"disambiguationData":[TD([[makeQuery(id+"F0.imprint","IMPRINT",EDGE,{"derivedFrom":sQuery(id+"F0.wireOp",EDGE,"E478.MirrorCS")}),-1.0]])]});
            var Q6;
            {var subQ14=sQuery(id+"F0.wireOp",EDGE,"E365");Q6=makeQuery(id+"F0.imprint","IMPRINT",FACE,{"disambiguationData":[TD([[makeQuery(id+"F0.imprint","IMPRINT",EDGE,{"derivedFrom":subQ14}),-1.0]])]});}
            var Q7;
            Q7=makeQuery(id+"F0.imprint","IMPRINT",FACE,{"disambiguationData":[TD([[makeQuery(id+"F0.imprint","IMPRINT",EDGE,{"derivedFrom":sQuery(id+"F0.wireOp",EDGE,"E362")}),-1.0]])]});
            var Q8;
            Q8=makeQuery(id+"F0.imprint","IMPRINT",FACE,{"disambiguationData":[TD([[makeQuery(id+"F0.imprint","IMPRINT",EDGE,{"derivedFrom":sQuery(id+"F0.wireOp",EDGE,"E476.MirrorCS")}),-1.0]])]});
            var Q9;
            Q9=makeQuery(id+"F0.imprint","IMPRINT",FACE,{"disambiguationData":[TD([[makeQuery(id+"F0.imprint","IMPRINT",EDGE,{"derivedFrom":sQuery(id+"F0.wireOp",EDGE,"E340.MirrorCS")}),1.0]])]});
            var Q10;
            Q10=makeQuery(id+"F0.imprint","IMPRINT",FACE,{"disambiguationData":[TD([[makeQuery(id+"F0.imprint","IMPRINT",EDGE,{"derivedFrom":sQuery(id+"F0.wireOp",EDGE,"E439.MirrorCS")}),1.0]])]});
            var Q11;
            Q11=makeQuery(id+"F0.imprint","IMPRINT",FACE,{"disambiguationData":[TD([[makeQuery(id+"F0.imprint","IMPRINT",EDGE,{"derivedFrom":sQuery(id+"F0.wireOp",EDGE,"E371")}),-1.0]])]});
            var Q12;
            {var subQ30=sQuery(id+"F0.wireOp",EDGE,"E405.MirrorCS");Q12=makeQuery(id+"F0.imprint","IMPRINT",FACE,{"disambiguationData":[TD([[makeQuery(id+"F0.imprint","IMPRINT",EDGE,{"derivedFrom":subQ30}),1.0]])]});}
            var Q13;
            {var subQ15=sQuery(id+"F0.wireOp",EDGE,"E481.MirrorCS");Q13=makeQuery(id+"F0.imprint","IMPRINT",FACE,{"disambiguationData":[TD([[makeQuery(id+"F0.imprint","IMPRINT",EDGE,{"derivedFrom":subQ15}),-1.0]])]});}
            var Q14;
            Q14=makeQuery(id+"F0.imprint","IMPRINT",FACE,{"disambiguationData":[TD([[makeQuery(id+"F0.imprint","IMPRINT",EDGE,{"derivedFrom":sQuery(id+"F0.wireOp",EDGE,"E399.MirrorCS")}),1.0]])]});
            var Q15;
            Q15=makeQuery(id+"F0.imprint","IMPRINT",FACE,{"disambiguationData":[TD([[makeQuery(id+"F0.imprint","IMPRINT",EDGE,{"derivedFrom":sQuery(id+"F0.wireOp",EDGE,"E398.MirrorCS")}),1.0]])]});
            var Q16;
            Q16=makeQuery(id+"F0.imprint","IMPRINT",FACE,{"disambiguationData":[TD([[makeQuery(id+"F0.imprint","IMPRINT",EDGE,{"derivedFrom":sQuery(id+"F0.wireOp",EDGE,"E438.MirrorCS")}),1.0]])]});
            var Q17;
            Q17=makeQuery(id+"F0.imprint","IMPRINT",FACE,{"disambiguationData":[TD([[makeQuery(id+"F0.imprint","IMPRINT",EDGE,{"derivedFrom":sQuery(id+"F0.wireOp",EDGE,"E389")}),-1.0]])]});
            var Q18;
            Q18=makeQuery(id+"F0.imprint","IMPRINT",FACE,{"disambiguationData":[TD([[makeQuery(id+"F0.imprint","IMPRINT",EDGE,{"derivedFrom":sQuery(id+"F0.wireOp",EDGE,"E437.MirrorCS")}),1.0]])]});
            var Q19;
            {var subQ0=sQuery(id+"F0.wireOp",EDGE,"E338");var subQ1=sQuery(id+"F0.wireOp",EDGE,"E2");var subQ2=makeQuery(id+"F0.imprint","INTERSECT",VERTEX,{"disambiguationData":[OD(0.0)],"derivedFrom":[subQ1,subQ0]});Q19=makeQuery(id+"F0.imprint","IMPRINT",FACE,{"disambiguationData":[TD([[makeQuery(id+"F0.imprint","IMPRINT",EDGE,{"disambiguationData":[TD([[subQ2,1.0]])],"derivedFrom":subQ1}),1.0]])]});}
            var Q20;
            {var subQ0=sQuery(id+"F0.wireOp",EDGE,"E339");var subQ1=sQuery(id+"F0.wireOp",EDGE,"E2");var subQ2=makeQuery(id+"F0.imprint","INTERSECT",VERTEX,{"disambiguationData":[OD(0.0)],"derivedFrom":[subQ1,subQ0]});Q20=makeQuery(id+"F0.imprint","IMPRINT",FACE,{"disambiguationData":[TD([[makeQuery(id+"F0.imprint","IMPRINT",EDGE,{"disambiguationData":[TD([[subQ2,-1.0]])],"derivedFrom":subQ1}),1.0]])]});}
            var Q21;
            Q21=makeQuery(id+"F0.imprint","IMPRINT",FACE,{"disambiguationData":[TD([[makeQuery(id+"F0.imprint","IMPRINT",EDGE,{"derivedFrom":sQuery(id+"F0.wireOp",EDGE,"E380")}),-1.0]])]});
            var Q22;
            {var subQ0=sQuery(id+"F0.wireOp",EDGE,"E338");var subQ1=sQuery(id+"F0.wireOp",EDGE,"E2");var subQ2=makeQuery(id+"F0.imprint","INTERSECT",VERTEX,{"disambiguationData":[OD(1.0)],"derivedFrom":[subQ1,subQ0]});Q22=makeQuery(id+"F0.imprint","IMPRINT",FACE,{"disambiguationData":[TD([[makeQuery(id+"F0.imprint","IMPRINT",EDGE,{"disambiguationData":[TD([[subQ2,-1.0]])],"derivedFrom":subQ1}),1.0]])]});}
            var Q23;
            {var subQ0=sQuery(id+"F0.wireOp",EDGE,"E405.MirrorCS");Q23=makeQuery(id+"F0.imprint","IMPRINT",FACE,{"disambiguationData":[TD([[makeQuery(id+"F0.imprint","IMPRINT",EDGE,{"derivedFrom":subQ0}),-1.0]])]});}
            var Q24;
            {var subQ0=sQuery(id+"F0.wireOp",EDGE,"E3");var subQ1=sQuery(id+"F0.wireOp",EDGE,"E338");var subQ2=makeQuery(id+"F0.imprint","INTERSECT",VERTEX,{"disambiguationData":[OD(1.0)],"derivedFrom":[subQ1,subQ0]});Q24=makeQuery(id+"F0.imprint","IMPRINT",FACE,{"disambiguationData":[TD([[makeQuery(id+"F0.imprint","IMPRINT",EDGE,{"disambiguationData":[TD([[subQ2,1.0]])],"derivedFrom":subQ1}),-1.0]])]});}
            var Q25;
            {var subQ0=sQuery(id+"F0.wireOp",EDGE,"E3");var subQ1=sQuery(id+"F0.wireOp",EDGE,"E339");var subQ2=makeQuery(id+"F0.imprint","INTERSECT",VERTEX,{"disambiguationData":[OD(0.0)],"derivedFrom":[subQ1,subQ0]});Q25=makeQuery(id+"F0.imprint","IMPRINT",FACE,{"disambiguationData":[TD([[makeQuery(id+"F0.imprint","IMPRINT",EDGE,{"disambiguationData":[TD([[subQ2,-1.0]])],"derivedFrom":subQ1}),1.0]])]});}
            var Q26;
            {var subQ0=sQuery(id+"F0.wireOp",EDGE,"E365");Q26=makeQuery(id+"F0.imprint","IMPRINT",FACE,{"disambiguationData":[TD([[makeQuery(id+"F0.imprint","IMPRINT",EDGE,{"derivedFrom":subQ0}),1.0]])]});}
            var Q27;
            {var subQ0=sQuery(id+"F0.wireOp",EDGE,"E392");Q27=makeQuery(id+"F0.imprint","IMPRINT",FACE,{"disambiguationData":[TD([[makeQuery(id+"F0.imprint","IMPRINT",EDGE,{"derivedFrom":subQ0}),1.0]])]});}
            var Q28;
            {var subQ0=sQuery(id+"F0.wireOp",EDGE,"E411.MirrorCS");Q28=makeQuery(id+"F0.imprint","IMPRINT",FACE,{"disambiguationData":[TD([[makeQuery(id+"F0.imprint","IMPRINT",EDGE,{"derivedFrom":subQ0}),-1.0]])]});}
            var Q29;
            {var subQ0=sQuery(id+"F0.wireOp",EDGE,"E445.MirrorCS");Q29=makeQuery(id+"F0.imprint","IMPRINT",FACE,{"disambiguationData":[TD([[makeQuery(id+"F0.imprint","IMPRINT",EDGE,{"derivedFrom":subQ0}),-1.0]])]});}
            var Q30;
            {var subQ0=sQuery(id+"F0.wireOp",EDGE,"E485.MirrorCS");Q30=makeQuery(id+"F0.imprint","IMPRINT",FACE,{"disambiguationData":[TD([[makeQuery(id+"F0.imprint","IMPRINT",EDGE,{"derivedFrom":subQ0}),1.0]])]});}
            var Q31;
            {var subQ0=sQuery(id+"F0.wireOp",EDGE,"E339");var subQ1=sQuery(id+"F0.wireOp",EDGE,"E2");var subQ2=makeQuery(id+"F0.imprint","INTERSECT",VERTEX,{"disambiguationData":[OD(0.0)],"derivedFrom":[subQ1,subQ0]});Q31=makeQuery(id+"F0.imprint","IMPRINT",FACE,{"disambiguationData":[TD([[makeQuery(id+"F0.imprint","IMPRINT",EDGE,{"disambiguationData":[TD([[subQ2,1.0]])],"derivedFrom":subQ1}),1.0]])]});}
            var Q32;
            {var subQ0=sQuery(id+"F0.wireOp",EDGE,"E3");var subQ1=sQuery(id+"F0.wireOp",EDGE,"E338");var subQ2=makeQuery(id+"F0.imprint","INTERSECT",VERTEX,{"disambiguationData":[OD(1.0)],"derivedFrom":[subQ1,subQ0]});Q32=makeQuery(id+"F0.imprint","IMPRINT",FACE,{"disambiguationData":[TD([[makeQuery(id+"F0.imprint","IMPRINT",EDGE,{"disambiguationData":[TD([[subQ2,1.0]])],"derivedFrom":subQ1}),1.0]])]});}
            var Q33;
            {var subQ0=sQuery(id+"F0.wireOp",EDGE,"E3");var subQ1=sQuery(id+"F0.wireOp",EDGE,"E338");var subQ2=makeQuery(id+"F0.imprint","INTERSECT",VERTEX,{"disambiguationData":[OD(0.0)],"derivedFrom":[subQ1,subQ0]});Q33=makeQuery(id+"F0.imprint","IMPRINT",FACE,{"disambiguationData":[TD([[makeQuery(id+"F0.imprint","IMPRINT",EDGE,{"disambiguationData":[TD([[subQ2,-1.0]])],"derivedFrom":subQ1}),1.0]])]});}
            var Q34;
            {var subQ0=sQuery(id+"F0.wireOp",EDGE,"E3");var subQ1=sQuery(id+"F0.wireOp",EDGE,"E339");var subQ2=makeQuery(id+"F0.imprint","INTERSECT",VERTEX,{"disambiguationData":[OD(0.0)],"derivedFrom":[subQ1,subQ0]});Q34=makeQuery(id+"F0.imprint","IMPRINT",FACE,{"disambiguationData":[TD([[makeQuery(id+"F0.imprint","IMPRINT",EDGE,{"disambiguationData":[TD([[subQ2,-1.0]])],"derivedFrom":subQ1}),-1.0]])]});}
            var Q35;
            {var subQ0=sQuery(id+"F0.wireOp",EDGE,"E383");Q35=makeQuery(id+"F0.imprint","IMPRINT",FACE,{"disambiguationData":[TD([[makeQuery(id+"F0.imprint","IMPRINT",EDGE,{"derivedFrom":subQ0}),1.0]])]});}
            var Q36;
            {var subQ0=sQuery(id+"F0.wireOp",EDGE,"E481.MirrorCS");Q36=makeQuery(id+"F0.imprint","IMPRINT",FACE,{"disambiguationData":[TD([[makeQuery(id+"F0.imprint","IMPRINT",EDGE,{"derivedFrom":subQ0}),1.0]])]});}
            var Q37;
            {var subQ0=sQuery(id+"F0.wireOp",EDGE,"E326.filletArc");var subQ1=sQuery(id+"F0.wireOp",EDGE,"E323");var subQ2=makeQuery(id+"F0.imprint","INTERSECT",VERTEX,{"derivedFrom":[subQ1,subQ0]});Q37=makeQuery(id+"F0.imprint","IMPRINT",FACE,{"disambiguationData":[TD([[makeQuery(id+"F0.imprint","IMPRINT",EDGE,{"disambiguationData":[TD([[subQ2,1.0]])],"derivedFrom":subQ1}),1.0]])]});}
            var Q38;
            {var subQ0=sQuery(id+"F0.wireOp",EDGE,"E327.filletArc");var subQ1=sQuery(id+"F0.wireOp",EDGE,"E323");var subQ2=makeQuery(id+"F0.imprint","INTERSECT",VERTEX,{"derivedFrom":[subQ1,subQ0]});Q38=makeQuery(id+"F0.imprint","IMPRINT",FACE,{"disambiguationData":[TD([[makeQuery(id+"F0.imprint","IMPRINT",EDGE,{"disambiguationData":[TD([[subQ2,-1.0]])],"derivedFrom":subQ1}),1.0]])]});}
            var Q39;
            {var subQ0=sQuery(id+"F0.wireOp",EDGE,"E488.MirrorCS");Q39=makeQuery(id+"F0.imprint","IMPRINT",FACE,{"disambiguationData":[TD([[makeQuery(id+"F0.imprint","IMPRINT",EDGE,{"derivedFrom":subQ0}),1.0]])]});}
            var Q40;
            {var subQ0=sQuery(id+"F0.wireOp",EDGE,"E3");var subQ1=sQuery(id+"F0.wireOp",EDGE,"E338");var subQ2=makeQuery(id+"F0.imprint","INTERSECT",VERTEX,{"disambiguationData":[OD(0.0)],"derivedFrom":[subQ1,subQ0]});Q40=makeQuery(id+"F0.imprint","IMPRINT",FACE,{"disambiguationData":[TD([[makeQuery(id+"F0.imprint","IMPRINT",EDGE,{"disambiguationData":[TD([[subQ2,-1.0]])],"derivedFrom":subQ1}),-1.0]])]});}
            var Q41;
            {var subQ0=sQuery(id+"F0.wireOp",EDGE,"E444.MirrorCS");Q41=makeQuery(id+"F0.imprint","IMPRINT",FACE,{"disambiguationData":[TD([[makeQuery(id+"F0.imprint","IMPRINT",EDGE,{"derivedFrom":subQ0}),-1.0]])]});}
            var Q42;
            {var subQ0=sQuery(id+"F0.wireOp",EDGE,"E414.MirrorCS");Q42=makeQuery(id+"F0.imprint","IMPRINT",FACE,{"disambiguationData":[TD([[makeQuery(id+"F0.imprint","IMPRINT",EDGE,{"derivedFrom":subQ0}),-1.0]])]});}
            var Q43;
            {var subQ0=sQuery(id+"F0.wireOp",EDGE,"E443.MirrorCS");Q43=makeQuery(id+"F0.imprint","IMPRINT",FACE,{"disambiguationData":[TD([[makeQuery(id+"F0.imprint","IMPRINT",EDGE,{"derivedFrom":subQ0}),-1.0]])]});}
            extrude(context, id + "F2", {"entities" : qUnion([Q0, Q1, Q2, Q3, Q4, Q5, Q6, Q7, Q8, Q9, Q10, Q11, Q12, Q13, Q14, Q15, Q16, Q17, Q18, Q19, Q20, Q21, Q22, Q23, Q24, Q25, Q26, Q27, Q28, Q29, Q30, Q31, Q32, Q33, Q34, Q35, Q36, Q37, Q38, Q39, Q40, Q41, Q42, Q43]), "depth" : 6.35 * mm});
        }
    });
